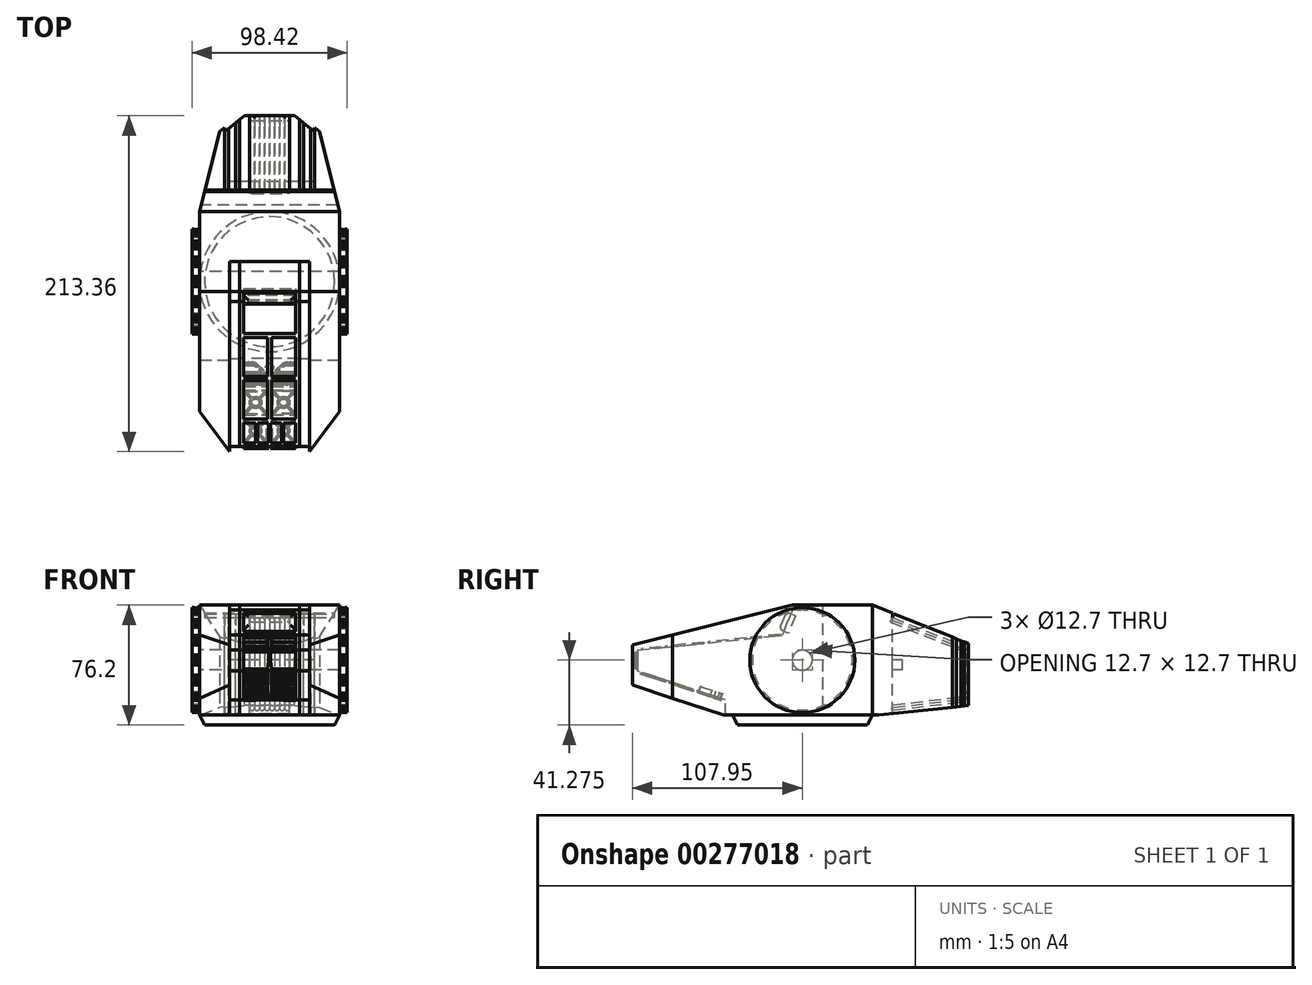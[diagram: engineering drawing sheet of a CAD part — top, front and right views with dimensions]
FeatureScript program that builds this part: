
annotation { "Feature Type Name" : "Feature", "Feature Type Description" : "" }
export const myFeature = defineFeature(function(context is Context, id is Id, definition is map)
    precondition{}
    {
        {
            var Q0;
            Q0=qCreatedBy(makeId("Top.planeOp"),FACE);
            cPlane(context, id + "F0", {"entities" : qUnion([Q0]), "cplaneType" : CPlaneType.OFFSET, "offset" : 38.1 * mm, "width" : 152.4 * mm, "height" : 152.4 * mm});
        }
        {
            var Q0;
            Q0=qCreatedBy(makeId("Front.planeOp"),FACE);
            cPlane(context, id + "F1", {"entities" : qUnion([Q0]), "cplaneType" : CPlaneType.OFFSET, "offset" : 165.1 * mm, "oppositeDirection" : true, "width" : 152.4 * mm, "height" : 152.4 * mm});
        }
        {
            var Q0;
            Q0=qCreatedBy(makeId("Top.planeOp"),FACE);
            cPlane(context, id + "F2", {"entities" : qUnion([Q0]), "cplaneType" : CPlaneType.OFFSET, "offset" : 38.1 * mm, "width" : 152.4 * mm, "height" : 152.4 * mm});
        }
        {
            var Q0;
            Q0=qCreatedBy(makeId("Right.planeOp"),FACE);
            cPlane(context, id + "F3", {"entities" : qUnion([Q0]), "cplaneType" : CPlaneType.OFFSET, "offset" : 44.45 * mm, "width" : 152.4 * mm, "height" : 152.4 * mm});
        }
        {
            var Q0;
            Q0=qCreatedBy(makeId("Top.planeOp"),FACE);
            cPlane(context, id + "F4", {"entities" : qUnion([Q0]), "cplaneType" : CPlaneType.OFFSET, "offset" : 38.1 * mm, "oppositeDirection" : true, "width" : 152.4 * mm, "height" : 152.4 * mm});
        }
        {
            var Q0;
            Q0=qCreatedBy(id+"F4.planeOp",FACE);
            cPlane(context, id + "F5", {"entities" : qUnion([Q0]), "cplaneType" : CPlaneType.OFFSET, "offset" : 6.35 * mm, "width" : 152.4 * mm, "height" : 152.4 * mm});
        }
        {
            var Q0;
            Q0=qCreatedBy(makeId("Top.planeOp"),FACE);
            var sketch = newSketch(context, id + "F6", { "sketchPlane" : qUnion([Q0])});
            skLineSegment(sketch, "E0", {"start": v(-19.05, 0) * mm, "end": v(19.05, 0) * mm});
            skLineSegment(sketch, "E1", {"start": v(0, 0) * mm, "end": v(0, 45.8) * mm});
            skPoint(sketch, "E1.endSnap0", {"position": v(0, 0) * mm});
            skLineSegment(sketch, "E2", {"start": v(-44.45, 25.4) * mm, "end": v(-44.45, 152.4) * mm});
            skLineSegment(sketch, "E3", {"start": v(44.45, 25.4) * mm, "end": v(44.45, 152.4) * mm});
            skLineSegment(sketch, "E4", {"start": v(-44.45, 152.4) * mm, "end": v(44.45, 152.4) * mm});
            skLineSegment(sketch, "E5", {"start": v(0, 152.4) * mm, "end": v(0, 215.9) * mm});
            skPoint(sketch, "E5.endSnap0", {"position": v(0, 152.4) * mm});
            skLineSegment(sketch, "E6", {"start": v(-15.88, 215.9) * mm, "end": v(15.87, 215.9) * mm});
            skLineSegment(sketch, "E7.0", {"start": v(-31.75, 203.2) * mm, "end": v(31.75, 203.2) * mm});
            skLineSegment(sketch, "E8", {"start": v(-44.45, 152.4) * mm, "end": v(-31.75, 203.2) * mm});
            skLineSegment(sketch, "E9", {"start": v(-15.88, 215.9) * mm, "end": v(-31.75, 203.2) * mm});
            skLineSegment(sketch, "E10", {"start": v(15.87, 215.9) * mm, "end": v(31.75, 203.2) * mm});
            skLineSegment(sketch, "E11", {"start": v(31.75, 203.2) * mm, "end": v(44.45, 152.4) * mm});
            skLineSegment(sketch, "E12", {"start": v(-19.05, 0) * mm, "end": v(-19.05, 120.65) * mm});
            skLineSegment(sketch, "E13", {"start": v(-19.05, 120.65) * mm, "end": v(19.05, 120.65) * mm});
            skLineSegment(sketch, "E14", {"start": v(19.05, 120.65) * mm, "end": v(19.05, 0) * mm});
            skLineSegment(sketch, "E15", {"start": v(-44.45, 25.4) * mm, "end": v(-25.4, 0) * mm});
            skLineSegment(sketch, "E16", {"start": v(19.05, 0) * mm, "end": v(25.4, 0) * mm});
            skLineSegment(sketch, "E17", {"start": v(25.4, 0) * mm, "end": v(44.45, 25.4) * mm});
            skLineSegment(sketch, "E18", {"start": v(-25.4, 0) * mm, "end": v(-19.05, 0) * mm});
            skSolve(sketch);
        }
        {
            var Q0;
            {var subQ1=sQuery(id+"F6.wireOp",EDGE,"E2");Q0=makeQuery(id+"F6.imprint","IMPRINT",FACE,{"disambiguationData":[TD([[makeQuery(id+"F6.imprint","IMPRINT",EDGE,{"derivedFrom":subQ1}),-1.0]])]});}
            extrude(context, id + "F7", {"entities" : qUnion([Q0]), "depth" : 76.2 * mm, "symmetric" : true});
        }
        {
            var Q0;
            Q0=qCreatedBy(makeId("Right.planeOp"),FACE);
            var sketch = newSketch(context, id + "F8", { "sketchPlane" : qUnion([Q0])});
            skLineSegment(sketch, "E19", {"start": v(0, 0) * mm, "end": v(101.6, 0) * mm});
            skLineSegment(sketch, "E20", {"start": v(101.6, 38.1) * mm, "end": v(101.6, -38.51) * mm});
            skLineSegment(sketch, "E21", {"start": v(0, 12.7) * mm, "end": v(0, -12.7) * mm});
            skLineSegment(sketch, "E22", {"start": v(0, 0) * mm, "end": v(107.95, 0) * mm});
            skLineSegment(sketch, "E23", {"start": v(107.95, 0) * mm, "end": v(107.95, -11.67) * mm});
            skLineSegment(sketch, "E24", {"start": v(63.5, -11.67) * mm, "end": v(152.4, -11.67) * mm});
            skLineSegment(sketch, "E25", {"start": v(63.5, -38.51) * mm, "end": v(59.18, -32.16) * mm});
            skLineSegment(sketch, "E26", {"start": v(0, -12.7) * mm, "end": v(59.18, -32.16) * mm});
            skLineSegment(sketch, "E27", {"start": v(0, 12.7) * mm, "end": v(101.6, 38.1) * mm});
            skLineSegment(sketch, "E28", {"start": v(152.4, -38.1) * mm, "end": v(156.72, -31.75) * mm});
            skLineSegment(sketch, "E29", {"start": v(152.4, 38.1) * mm, "end": v(215.9, 12.7) * mm});
            skLineSegment(sketch, "E30", {"start": v(156.72, -31.75) * mm, "end": v(215.9, -25.4) * mm});
            skLineSegment(sketch, "E31", {"start": v(215.9, -25.4) * mm, "end": v(215.9, 12.7) * mm});
            skLineSegment(sketch, "E32.bottom", {"start": v(0, 38.1) * mm, "end": v(215.9, 38.1) * mm});
            skLineSegment(sketch, "E32.top", {"start": v(0, -38.1) * mm, "end": v(215.9, -38.1) * mm});
            skLineSegment(sketch, "E32.left", {"start": v(0, 38.1) * mm, "end": v(0, -38.1) * mm});
            skLineSegment(sketch, "E32.right", {"start": v(215.9, 38.1) * mm, "end": v(215.9, -38.1) * mm});
            skLineSegment(sketch, "E33", {"start": v(215.9, 12.7) * mm, "end": v(215.9, -25.4) * mm});
            skLineSegment(sketch, "E34", {"start": v(152.4, 38.1) * mm, "end": v(156.72, -31.75) * mm});
            skLineSegment(sketch, "E35", {"start": v(221.8, 0) * mm, "end": v(221.8, 12.7) * mm});
            skPoint(sketch, "E35.startSnap0", {"position": v(215.9, 0) * mm});
            skLineSegment(sketch, "E36", {"start": v(221.8, 0) * mm, "end": v(221.8, -25.4) * mm});
            skLineSegment(sketch, "E37", {"start": v(63.5, -38.51) * mm, "end": v(63.5, -43.93) * mm});
            skLineSegment(sketch, "E38", {"start": v(63.5, -43.93) * mm, "end": v(152.4, -43.93) * mm});
            skLineSegment(sketch, "E39", {"start": v(107.95, -43.93) * mm, "end": v(107.95, 70.13) * mm});
            skLineSegment(sketch, "E40", {"start": v(59.18, -32.16) * mm, "end": v(156.72, -31.75) * mm});
            skSolve(sketch);
        }
        {
            var Q0;
            {var subQ0=sQuery(id+"F6.wireOp",EDGE,"E12");Q0=makeQuery(id+"F6.imprint","IMPRINT",FACE,{"disambiguationData":[TD([[makeQuery(id+"F6.imprint","IMPRINT",EDGE,{"derivedFrom":subQ0}),-1.0]])]});}
            extrude(context, id + "F9", {"entities" : qUnion([Q0]), "depth" : 76.2 * mm, "symmetric" : true});
        }
        {
            var Q0;
            {var subQ5=sQuery(id+"F6.wireOp",EDGE,"E9");Q0=makeQuery(id+"F6.imprint","IMPRINT",FACE,{"disambiguationData":[TD([[makeQuery(id+"F6.imprint","IMPRINT",EDGE,{"derivedFrom":subQ5}),1.0]])]});}
            var Q1;
            {var subQ5=sQuery(id+"F6.wireOp",EDGE,"E10");Q1=makeQuery(id+"F6.imprint","IMPRINT",FACE,{"disambiguationData":[TD([[makeQuery(id+"F6.imprint","IMPRINT",EDGE,{"derivedFrom":subQ5}),-1.0]])]});}
            var Q2;
            {var subQ0=sQuery(id+"F6.wireOp",EDGE,"E8");Q2=makeQuery(id+"F6.imprint","IMPRINT",FACE,{"disambiguationData":[TD([[makeQuery(id+"F6.imprint","IMPRINT",EDGE,{"derivedFrom":subQ0}),-1.0]])]});}
            var Q3;
            {var subQ0=sQuery(id+"F6.wireOp",EDGE,"E11");Q3=makeQuery(id+"F6.imprint","IMPRINT",FACE,{"disambiguationData":[TD([[makeQuery(id+"F6.imprint","IMPRINT",EDGE,{"derivedFrom":subQ0}),-1.0]])]});}
            extrude(context, id + "F10", {"entities" : qUnion([Q0, Q1, Q2, Q3]), "depth" : 76.2 * mm, "symmetric" : true});
        }
        {
            var Q0;
            {var subQ0=sQuery(id+"F8.wireOp",EDGE,"E32.right");var subQ1=sQuery(id+"F8.wireOp",EDGE,"3308d05f-1129-43a6-b52a-610bf1bbaef7");var subQ2=makeQuery(id+"F8.imprint","INTERSECT",VERTEX,{"derivedFrom":[subQ1,subQ0]});Q0=makeQuery(id+"F8.imprint","IMPRINT",FACE,{"disambiguationData":[TD([[makeQuery(id+"F8.imprint","IMPRINT",EDGE,{"disambiguationData":[TD([[subQ2,1.0]])],"derivedFrom":subQ1}),1.0]])]});}
            var Q1;
            {var subQ6=sQuery(id+"F8.wireOp",EDGE,"E28");Q1=makeQuery(id+"F8.imprint","IMPRINT",FACE,{"disambiguationData":[TD([[makeQuery(id+"F8.imprint","IMPRINT",EDGE,{"derivedFrom":subQ6}),-1.0]])]});}
            var Q2;
            {var subQ0=sQuery(id+"F8.wireOp",EDGE,"E29");Q2=makeQuery(id+"F8.imprint","IMPRINT",FACE,{"disambiguationData":[TD([[makeQuery(id+"F8.imprint","IMPRINT",EDGE,{"derivedFrom":subQ0}),1.0]])]});}
            var Q3;
            {var subQ0=sQuery(id+"F8.wireOp",EDGE,"E27");Q3=makeQuery(id+"F8.imprint","IMPRINT",FACE,{"disambiguationData":[TD([[makeQuery(id+"F8.imprint","IMPRINT",EDGE,{"derivedFrom":subQ0}),1.0]])]});}
            var Q4;
            {var subQ0=sQuery(id+"F8.wireOp",EDGE,"E26");Q4=makeQuery(id+"F8.imprint","IMPRINT",FACE,{"disambiguationData":[TD([[makeQuery(id+"F8.imprint","IMPRINT",EDGE,{"derivedFrom":subQ0}),-1.0]])]});}
            extrude(context, id + "F11", {"entities" : qUnion([Q0, Q1, Q2, Q3, Q4]), "depth" : 101.6 * mm, "symmetric" : true});
        }
        {
            var Q0;
            Q0=makeQuery(id+"F11.opExtrude","SWEPT_BODY",BODY,{"disambiguationData":[OSD([sQuery(id+"F8.wireOp",EDGE,"E29"),sQuery(id+"F8.wireOp",EDGE,"E32.bottom"),sQuery(id+"F8.wireOp",EDGE,"E32.right")])]});
            var Q1;
            Q1=makeQuery(id+"F11.opExtrude","SWEPT_BODY",BODY,{"disambiguationData":[OSD([sQuery(id+"F8.wireOp",EDGE,"E28"),sQuery(id+"F8.wireOp",EDGE,"E30"),sQuery(id+"F8.wireOp",EDGE,"E31"),sQuery(id+"F8.wireOp",EDGE,"E32.top"),sQuery(id+"F8.wireOp",EDGE,"E32.right")])]});
            var Q2;
            Q2=makeQuery(id+"F11.opExtrude","SWEPT_BODY",BODY,{"disambiguationData":[OSD([sQuery(id+"F8.wireOp",EDGE,"E27"),sQuery(id+"F8.wireOp",EDGE,"E32.bottom"),sQuery(id+"F8.wireOp",EDGE,"E32.left")])]});
            var Q3;
            Q3=makeQuery(id+"F11.opExtrude","SWEPT_BODY",BODY,{"disambiguationData":[OSD([sQuery(id+"F8.wireOp",EDGE,"E25"),sQuery(id+"F8.wireOp",EDGE,"E26"),sQuery(id+"F8.wireOp",EDGE,"E32.top"),sQuery(id+"F8.wireOp",EDGE,"E32.left")])]});
            var Q4;
            Q4=makeQuery(id+"F7.opExtrude","SWEPT_BODY",BODY,{"disambiguationData":[OSD([sQuery(id+"F6.wireOp",EDGE,"E2"),sQuery(id+"F6.wireOp",EDGE,"E3"),sQuery(id+"F6.wireOp",EDGE,"E4"),sQuery(id+"F6.wireOp",EDGE,"E12"),sQuery(id+"F6.wireOp",EDGE,"E13"),sQuery(id+"F6.wireOp",EDGE,"E14"),sQuery(id+"F6.wireOp",EDGE,"E15"),sQuery(id+"F6.wireOp",EDGE,"E16"),sQuery(id+"F6.wireOp",EDGE,"E17"),sQuery(id+"F6.wireOp",EDGE,"E18")])]});
            var Q5;
            Q5=makeQuery(id+"F9.opExtrude","SWEPT_BODY",BODY,{"disambiguationData":[OSD([sQuery(id+"F6.wireOp",EDGE,"E0"),sQuery(id+"F6.wireOp",EDGE,"E12"),sQuery(id+"F6.wireOp",EDGE,"E13"),sQuery(id+"F6.wireOp",EDGE,"E14")])]});
            var Q6;
            Q6=makeQuery(id+"F10.opExtrude","SWEPT_BODY",BODY,{"disambiguationData":[OSD([sQuery(id+"F6.wireOp",EDGE,"E4"),sQuery(id+"F6.wireOp",EDGE,"E6"),sQuery(id+"F6.wireOp",EDGE,"E8"),sQuery(id+"F6.wireOp",EDGE,"E9"),sQuery(id+"F6.wireOp",EDGE,"E10"),sQuery(id+"F6.wireOp",EDGE,"E11")])]});
            booleanBodies(context, id + "F12", {"operationType" : BooleanOperationType.SUBTRACTION, "tools" : qUnion([Q0, Q1, Q2, Q3]), "targets" : qUnion([Q4, Q5, Q6])});
        }
        {
            var Q0;
            Q0=qCreatedBy(makeId("Right.planeOp"),FACE);
            var sketch = newSketch(context, id + "F13", { "sketchPlane" : qUnion([Q0])});
            skLineSegment(sketch, "E41", {"start": v(3.17, 9.52) * mm, "end": v(95.25, 19.05) * mm});
            skLineSegment(sketch, "E42", {"start": v(101.6, 34.93) * mm, "end": v(95.25, 19.05) * mm});
            skLineSegment(sketch, "E43", {"start": v(101.6, 34.93) * mm, "end": v(120.65, 38.1) * mm});
            skLineSegment(sketch, "E44", {"start": v(3.17, 9.52) * mm, "end": v(3.17, -3.72) * mm});
            skLineSegment(sketch, "E45.0", {"start": v(59.18, -22.14) * mm, "end": v(2.98, -3.65) * mm});
            skLineSegment(sketch, "E46", {"start": v(59.18, -32.06) * mm, "end": v(59.18, -22.14) * mm});
            skLineSegment(sketch, "E47", {"start": v(120.65, 38.1) * mm, "end": v(0, 40.38) * mm});
            skLineSegment(sketch, "E48", {"start": v(0, 40.38) * mm, "end": v(0, -32.06) * mm});
            skLineSegment(sketch, "E49", {"start": v(0, -32.06) * mm, "end": v(59.18, -32.06) * mm});
            skSolve(sketch);
        }
        {
            var Q0;
            Q0 = qSketchRegion(id + "F13", true);
            extrude(context, id + "F14", {"entities" : qUnion([Q0]), "operationType" : NewBodyOperationType.REMOVE, "depth" : 50.8 * mm, "symmetric" : true});
        }
        {
            var Q0;
            Q0=qCreatedBy(id+"F0.planeOp",FACE);
            var sketch = newSketch(context, id + "F15", { "sketchPlane" : qUnion([Q0])});
            skLineSegment(sketch, "E50", {"start": v(0, 0) * mm, "end": v(0, 165.1) * mm});
            skLineSegment(sketch, "E51", {"start": v(-44.45, 152.4) * mm, "end": v(74.49, 152.4) * mm});
            skLineSegment(sketch, "E52", {"start": v(-19.05, 213.36) * mm, "end": v(-19.05, 165.1) * mm});
            skLineSegment(sketch, "E53", {"start": v(-21.6, 211.33) * mm, "end": v(-21.6, 165.1) * mm});
            skLineSegment(sketch, "E54", {"start": v(-28.58, 205.74) * mm, "end": v(-26.04, 207.77) * mm});
            skPoint(sketch, "E55.orphan", {"position": v(-28.58, 259.23) * mm});
            skPoint(sketch, "E56.orphan", {"position": v(-26.04, 263.6) * mm});
            skPoint(sketch, "E57.orphan", {"position": v(-21.6, 218.8) * mm});
            skPoint(sketch, "E58.orphan", {"position": v(-19.05, 223.69) * mm});
            skLineSegment(sketch, "E59", {"start": v(-28.58, 165.1) * mm, "end": v(-26.04, 165.1) * mm});
            skPoint(sketch, "E60.orphan", {"position": v(-78.7, 165.1) * mm});
            skLineSegment(sketch, "E61.trimOffspring", {"start": v(-28.58, 165.1) * mm, "end": v(-28.58, 205.74) * mm});
            skLineSegment(sketch, "E62.trimOffspring", {"start": v(-26.04, 165.1) * mm, "end": v(-26.04, 207.77) * mm});
            skLineSegment(sketch, "E63.trimOffspring", {"start": v(-21.6, 165.1) * mm, "end": v(-19.05, 165.1) * mm});
            skPoint(sketch, "E64.orphan", {"position": v(-31.75, 203.2) * mm});
            skLineSegment(sketch, "E65.trimOffspring", {"start": v(-21.6, 211.33) * mm, "end": v(-19.05, 213.36) * mm});
            skPoint(sketch, "E66.orphan", {"position": v(-15.88, 215.9) * mm});
            skLineSegment(sketch, "E67.MirrorCS", {"start": v(19.05, 213.36) * mm, "end": v(19.05, 165.1) * mm});
            skLineSegment(sketch, "E68.MirrorCS", {"start": v(21.6, 211.33) * mm, "end": v(21.6, 165.1) * mm});
            skLineSegment(sketch, "E69.MirrorCS", {"start": v(26.04, 165.1) * mm, "end": v(26.04, 207.77) * mm});
            skLineSegment(sketch, "E70.MirrorCS", {"start": v(28.58, 165.1) * mm, "end": v(28.58, 205.74) * mm});
            skLineSegment(sketch, "E71.MirrorCS", {"start": v(21.6, 165.1) * mm, "end": v(19.05, 165.1) * mm});
            skLineSegment(sketch, "E72.MirrorCS", {"start": v(28.58, 165.1) * mm, "end": v(26.04, 165.1) * mm});
            skLineSegment(sketch, "E73", {"start": v(-12.7, 215.9) * mm, "end": v(-12.7, 165.1) * mm});
            skLineSegment(sketch, "E74.MirrorCS", {"start": v(12.7, 215.9) * mm, "end": v(12.7, 165.1) * mm});
            skLineSegment(sketch, "E75", {"start": v(-12.7, 165.1) * mm, "end": v(12.7, 165.1) * mm});
            skPoint(sketch, "E76.orphan", {"position": v(-12.7, 158.24) * mm});
            skPoint(sketch, "E77.orphan", {"position": v(12.7, 158.24) * mm});
            skPoint(sketch, "E78.orphan", {"position": v(0, 215.9) * mm});
            skLineSegment(sketch, "E79", {"start": v(-12.7, 215.9) * mm, "end": v(12.7, 215.9) * mm});
            skLineSegment(sketch, "E80", {"start": v(19.05, 213.36) * mm, "end": v(21.6, 211.33) * mm});
            skLineSegment(sketch, "E81", {"start": v(26.04, 207.77) * mm, "end": v(28.58, 205.74) * mm});
            skSolve(sketch);
        }
        {
            var Q0;
            Q0 = qSketchRegion(id + "F15", true);
            extrude(context, id + "F16", {"entities" : qUnion([Q0]), "operationType" : NewBodyOperationType.REMOVE, "oppositeDirection" : true, "depth" : 76.2 * mm});
        }
        {
            var Q0;
            Q0 = qSketchRegion(id + "F15", true);
            extrude(context, id + "F17", {"entities" : qUnion([Q0]), "oppositeDirection" : true, "depth" : 76.2 * mm});
        }
        {
            var Q0;
            {var subQ0=sQuery(id+"F8.wireOp",EDGE,"E29");Q0=makeQuery(id+"F8.imprint","IMPRINT",FACE,{"disambiguationData":[TD([[makeQuery(id+"F8.imprint","IMPRINT",EDGE,{"derivedFrom":subQ0}),1.0]])]});}
            var Q1;
            {var subQ8=sQuery(id+"F8.wireOp",EDGE,"E28");Q1=makeQuery(id+"F8.imprint","IMPRINT",FACE,{"disambiguationData":[TD([[makeQuery(id+"F8.imprint","IMPRINT",EDGE,{"derivedFrom":subQ8}),-1.0]])]});}
            var Q2;
            {var subQ0=sQuery(id+"F8.wireOp",EDGE,"E32.right");var subQ1=sQuery(id+"F8.wireOp",EDGE,"3308d05f-1129-43a6-b52a-610bf1bbaef7");var subQ2=makeQuery(id+"F8.imprint","INTERSECT",VERTEX,{"derivedFrom":[subQ1,subQ0]});Q2=makeQuery(id+"F8.imprint","IMPRINT",FACE,{"disambiguationData":[TD([[makeQuery(id+"F8.imprint","IMPRINT",EDGE,{"disambiguationData":[TD([[subQ2,1.0]])],"derivedFrom":subQ1}),1.0]])]});}
            extrude(context, id + "F18", {"entities" : qUnion([Q0, Q1, Q2]), "depth" : 76.2 * mm, "symmetric" : true});
        }
        {
            var Q0;
            Q0=makeQuery(id+"F18.opExtrude","SWEPT_BODY",BODY,{"disambiguationData":[OSD([sQuery(id+"F8.wireOp",EDGE,"E29"),sQuery(id+"F8.wireOp",EDGE,"E32.bottom"),sQuery(id+"F8.wireOp",EDGE,"E32.right")])]});
            var Q1;
            Q1=makeQuery(id+"F18.opExtrude","SWEPT_BODY",BODY,{"disambiguationData":[OSD([sQuery(id+"F8.wireOp",EDGE,"E28"),sQuery(id+"F8.wireOp",EDGE,"E30"),sQuery(id+"F8.wireOp",EDGE,"E31"),sQuery(id+"F8.wireOp",EDGE,"E32.top"),sQuery(id+"F8.wireOp",EDGE,"E32.right")])]});
            var Q2;
            Q2=makeQuery(id+"F17.opExtrude","SWEPT_BODY",BODY,{"disambiguationData":[OSD([sQuery(id+"F15.wireOp",EDGE,"E54"),sQuery(id+"F15.wireOp",EDGE,"E59"),sQuery(id+"F15.wireOp",EDGE,"E61.trimOffspring"),sQuery(id+"F15.wireOp",EDGE,"E62.trimOffspring")])]});
            var Q3;
            Q3=makeQuery(id+"F17.opExtrude","SWEPT_BODY",BODY,{"disambiguationData":[OSD([sQuery(id+"F15.wireOp",EDGE,"E52"),sQuery(id+"F15.wireOp",EDGE,"E53"),sQuery(id+"F15.wireOp",EDGE,"E63.trimOffspring"),sQuery(id+"F15.wireOp",EDGE,"E65.trimOffspring")])]});
            var Q4;
            Q4=makeQuery(id+"F17.opExtrude","SWEPT_BODY",BODY,{"disambiguationData":[OSD([sQuery(id+"F15.wireOp",EDGE,"E73"),sQuery(id+"F15.wireOp",EDGE,"E74.MirrorCS"),sQuery(id+"F15.wireOp",EDGE,"E75"),sQuery(id+"F15.wireOp",EDGE,"E79")])]});
            var Q5;
            Q5=makeQuery(id+"F17.opExtrude","SWEPT_BODY",BODY,{"disambiguationData":[OSD([sQuery(id+"F15.wireOp",EDGE,"E67.MirrorCS"),sQuery(id+"F15.wireOp",EDGE,"E68.MirrorCS"),sQuery(id+"F15.wireOp",EDGE,"E71.MirrorCS"),sQuery(id+"F15.wireOp",EDGE,"E80")])]});
            var Q6;
            Q6=makeQuery(id+"F17.opExtrude","SWEPT_BODY",BODY,{"disambiguationData":[OSD([sQuery(id+"F15.wireOp",EDGE,"E69.MirrorCS"),sQuery(id+"F15.wireOp",EDGE,"E70.MirrorCS"),sQuery(id+"F15.wireOp",EDGE,"E72.MirrorCS"),sQuery(id+"F15.wireOp",EDGE,"E81")])]});
            booleanBodies(context, id + "F19", {"operationType" : BooleanOperationType.SUBTRACTION, "tools" : qUnion([Q0, Q1]), "targets" : qUnion([Q2, Q3, Q4, Q5, Q6])});
        }
        {
            var Q0;
            Q0=makeQuery(id+"F17.opExtrude","SWEPT_FACE",FACE,{"disambiguationData":[OSD([sQuery(id+"F15.wireOp",EDGE,"E75")])]});
            var sketch = newSketch(context, id + "F20", { "sketchPlane" : qUnion([Q0])});
            skLineSegment(sketch, "E82.bottom", {"start": v(28.58, -3.17) * mm, "end": v(-28.58, -3.18) * mm});
            skLineSegment(sketch, "E82.top", {"start": v(28.58, 3.18) * mm, "end": v(-28.58, 3.17) * mm});
            skLineSegment(sketch, "E82.left", {"start": v(28.58, -3.17) * mm, "end": v(28.58, 3.18) * mm});
            skLineSegment(sketch, "E82.right", {"start": v(-28.58, -3.18) * mm, "end": v(-28.58, 3.17) * mm});
            skPoint(sketch, "E82.middle", {"position": v(0, 0) * mm});
            skSolve(sketch);
        }
        {
            var Q0;
            Q0 = qSketchRegion(id + "F20", true);
            extrude(context, id + "F21", {"entities" : qUnion([Q0]), "oppositeDirection" : true, "depth" : 6.35 * mm});
        }
        {
            var Q0;
            Q0=qCreatedBy(id+"F1.planeOp",FACE);
            var sketch = newSketch(context, id + "F22", { "sketchPlane" : qUnion([Q0])});
            skLineSegment(sketch, "E83.bottom", {"start": v(28.58, 3.18) * mm, "end": v(-28.58, 3.18) * mm});
            skLineSegment(sketch, "E83.top", {"start": v(28.57, -3.18) * mm, "end": v(-28.58, -3.18) * mm});
            skLineSegment(sketch, "E83.left", {"start": v(28.57, 3.18) * mm, "end": v(28.57, -3.18) * mm});
            skLineSegment(sketch, "E83.right", {"start": v(-28.58, 3.18) * mm, "end": v(-28.58, -3.18) * mm});
            skPoint(sketch, "E83.middle", {"position": v(0, 0) * mm});
            skSolve(sketch);
        }
        {
            var Q0;
            Q0 = qSketchRegion(id + "F22", true);
            extrude(context, id + "F23", {"entities" : qUnion([Q0]), "oppositeDirection" : true, "depth" : 6.35 * mm});
        }
        {
            var Q0;
            Q0=makeQuery(id+"F23.opExtrude","SWEPT_BODY",BODY,{"disambiguationData":[OSD([sQuery(id+"F22.wireOp",EDGE,"E83.bottom"),sQuery(id+"F22.wireOp",EDGE,"E83.top"),sQuery(id+"F22.wireOp",EDGE,"E83.left"),sQuery(id+"F22.wireOp",EDGE,"E83.right")])]});
            var Q1;
            Q1=makeQuery(id+"F10.opExtrude","SWEPT_BODY",BODY,{"disambiguationData":[OSD([sQuery(id+"F6.wireOp",EDGE,"E4"),sQuery(id+"F6.wireOp",EDGE,"E6"),sQuery(id+"F6.wireOp",EDGE,"E8"),sQuery(id+"F6.wireOp",EDGE,"E9"),sQuery(id+"F6.wireOp",EDGE,"E10"),sQuery(id+"F6.wireOp",EDGE,"E11")])]});
            booleanBodies(context, id + "F24", {"operationType" : BooleanOperationType.SUBTRACTION, "tools" : qUnion([Q0]), "targets" : qUnion([Q1])});
        }
        {
            var Q0;
            Q0=qCreatedBy(id+"F2.planeOp",FACE);
            var sketch = newSketch(context, id + "F25", { "sketchPlane" : qUnion([Q0])});
            skLineSegment(sketch, "E84", {"start": v(15.87, 215.9) * mm, "end": v(-15.88, 215.9) * mm});
            skLineSegment(sketch, "E85", {"start": v(28.57, 205.74) * mm, "end": v(15.87, 215.9) * mm});
            skLineSegment(sketch, "E86", {"start": v(-15.88, 215.9) * mm, "end": v(-28.58, 205.74) * mm});
            skLineSegment(sketch, "E87", {"start": v(-28.58, 203.2) * mm, "end": v(-28.58, 205.74) * mm});
            skLineSegment(sketch, "E88.0", {"start": v(15.87, 213.36) * mm, "end": v(-15.88, 213.36) * mm});
            skLineSegment(sketch, "E89", {"start": v(28.57, 205.74) * mm, "end": v(28.57, 203.2) * mm});
            skLineSegment(sketch, "E90", {"start": v(-28.58, 203.2) * mm, "end": v(-15.88, 213.36) * mm});
            skLineSegment(sketch, "E91", {"start": v(15.87, 213.36) * mm, "end": v(28.57, 203.2) * mm});
            skSolve(sketch);
        }
        {
            var Q0;
            Q0=makeQuery(id+"F25.imprint","IMPRINT",FACE,{"disambiguationData":[TD([[makeQuery(id+"F25.imprint","IMPRINT",EDGE,{"derivedFrom":sQuery(id+"F25.wireOp",EDGE,"E84")}),1.0]])]});
            extrude(context, id + "F26", {"entities" : qUnion([Q0]), "operationType" : NewBodyOperationType.REMOVE, "endBound" : BoundingType.THROUGH_ALL, "oppositeDirection" : true, "depth" : 25.4 * mm});
        }
        {
            var Q0;
            Q0=qCreatedBy(id+"F3.planeOp",FACE);
            var sketch = newSketch(context, id + "F27", { "sketchPlane" : qUnion([Q0])});
            skLineSegment(sketch, "E92", {"start": v(215.9, -55.54) * mm, "end": v(165.1, -55.54) * mm});
            skLineSegment(sketch, "E93", {"start": v(165.1, -31.32) * mm, "end": v(165.1, 33.02) * mm});
            skLineSegment(sketch, "E94", {"start": v(215.9, 0) * mm, "end": v(215.9, 12.7) * mm});
            skLineSegment(sketch, "E95", {"start": v(215.9, 0) * mm, "end": v(215.9, -25.4) * mm});
            skLineSegment(sketch, "E96", {"start": v(0, 38.1) * mm, "end": v(152.4, 38.1) * mm});
            skLineSegment(sketch, "E97", {"start": v(165.1, 33.02) * mm, "end": v(215.9, 12.7) * mm});
            skLineSegment(sketch, "E98", {"start": v(0, -38.1) * mm, "end": v(157.1, -38.1) * mm});
            skLineSegment(sketch, "E99", {"start": v(157.1, -38.1) * mm, "end": v(157.1, -32.26) * mm});
            skLineSegment(sketch, "E100", {"start": v(165.1, -31.32) * mm, "end": v(215.9, -25.4) * mm});
            skPoint(sketch, "E101.orphan", {"position": v(0, 0) * mm});
            skLineSegment(sketch, "E102.0", {"start": v(165.1, 30.28) * mm, "end": v(209.37, 12.58) * mm});
            skLineSegment(sketch, "E103.0", {"start": v(165.1, -28.77) * mm, "end": v(207.75, -23.8) * mm});
            skLineSegment(sketch, "E104", {"start": v(214.96, 10.34) * mm, "end": v(215.9, 9.96) * mm});
            skLineSegment(sketch, "E105", {"start": v(215.6, -22.88) * mm, "end": v(215.9, -22.84) * mm});
            skLineSegment(sketch, "E106.0", {"start": v(213.36, 0) * mm, "end": v(213.36, -17.49) * mm});
            skLineSegment(sketch, "E107.0", {"start": v(213.36, 0) * mm, "end": v(213.36, 6.68) * mm});
            skLineSegment(sketch, "E108", {"start": v(165.1, 30.28) * mm, "end": v(164.16, 30.66) * mm});
            skLineSegment(sketch, "E109", {"start": v(165.1, 33.02) * mm, "end": v(164.16, 30.66) * mm});
            skLineSegment(sketch, "E110", {"start": v(165.1, 33.02) * mm, "end": v(168.5, 41.5) * mm});
            skLineSegment(sketch, "E111", {"start": v(168.5, 41.5) * mm, "end": v(156.55, 41.5) * mm});
            skLineSegment(sketch, "E112", {"start": v(156.55, 41.5) * mm, "end": v(156.55, -26.27) * mm});
            skLineSegment(sketch, "E113", {"start": v(165.1, -31.32) * mm, "end": v(165.43, -34.12) * mm});
            skLineSegment(sketch, "E114", {"start": v(165.43, -34.12) * mm, "end": v(156.55, -26.27) * mm});
            skPoint(sketch, "E115.trimOffspring.end.orphan", {"position": v(156.55, -29.76) * mm});
            skPoint(sketch, "E116.end.orphan", {"position": v(164.8, -28.77) * mm});
            skLineSegment(sketch, "E117", {"start": v(165.1, -31.32) * mm, "end": v(164.8, -28.77) * mm});
            skLineSegment(sketch, "E118", {"start": v(165.1, -28.77) * mm, "end": v(164.8, -28.8) * mm});
            skLineSegment(sketch, "E119", {"start": v(165.1, 30.28) * mm, "end": v(169.41, 41.07) * mm});
            skLineSegment(sketch, "E120", {"start": v(169.41, 41.07) * mm, "end": v(168.5, 41.5) * mm});
            skPoint(sketch, "E121.newPointB", {"position": v(213.36, 10.98) * mm});
            skArc(sketch, "E121.filletArc", {"start": v(213.36, 6.68) * mm, "mid": v(212.27, 10.24) * mm, "end": v(209.37, 12.58) * mm});
            skPoint(sketch, "E122.newPointB", {"position": v(213.36, -23.14) * mm});
            skArc(sketch, "E122.filletArc", {"start": v(207.75, -23.8) * mm, "mid": v(211.75, -21.7) * mm, "end": v(213.36, -17.49) * mm});
            skSolve(sketch);
        }
        {
            var Q0;
            {var subQ1=sQuery(id+"F27.wireOp",EDGE,"E97");Q0=makeQuery(id+"F27.imprint","IMPRINT",FACE,{"disambiguationData":[TD([[makeQuery(id+"F27.imprint","IMPRINT",EDGE,{"derivedFrom":subQ1}),-1.0]])]});}
            var Q1;
            {var subQ1=sQuery(id+"F27.wireOp",EDGE,"E100");Q1=makeQuery(id+"F27.imprint","IMPRINT",FACE,{"disambiguationData":[TD([[makeQuery(id+"F27.imprint","IMPRINT",EDGE,{"derivedFrom":subQ1}),1.0]])]});}
            var Q2;
            {var subQ8=sQuery(id+"F27.wireOp",EDGE,"E104");Q2=makeQuery(id+"F27.imprint","IMPRINT",FACE,{"disambiguationData":[TD([[makeQuery(id+"F27.imprint","IMPRINT",EDGE,{"derivedFrom":subQ8}),1.0]])]});}
            var Q3;
            {var subQ6=sQuery(id+"F27.wireOp",EDGE,"E104");Q3=makeQuery(id+"F27.imprint","IMPRINT",FACE,{"disambiguationData":[TD([[makeQuery(id+"F27.imprint","IMPRINT",EDGE,{"derivedFrom":subQ6}),-1.0]])]});}
            extrude(context, id + "F28", {"entities" : qUnion([Q0, Q1, Q2, Q3]), "operationType" : NewBodyOperationType.REMOVE, "endBound" : BoundingType.THROUGH_ALL, "oppositeDirection" : true, "depth" : 25.4 * mm});
        }
        {
            var Q0;
            {var subQ0=sQuery(id+"F27.wireOp",EDGE,"E108");Q0=makeQuery(id+"F27.imprint","IMPRINT",FACE,{"disambiguationData":[TD([[makeQuery(id+"F27.imprint","IMPRINT",EDGE,{"derivedFrom":subQ0}),1.0]])]});}
            var Q1;
            {var subQ0=sQuery(id+"F27.wireOp",EDGE,"E110");Q1=makeQuery(id+"F27.imprint","IMPRINT",FACE,{"disambiguationData":[TD([[makeQuery(id+"F27.imprint","IMPRINT",EDGE,{"derivedFrom":subQ0}),-1.0]])]});}
            extrude(context, id + "F29", {"entities" : qUnion([Q0, Q1]), "oppositeDirection" : true, "depth" : 88.9 * mm});
        }
        {
            var Q0;
            Q0=makeQuery(id+"F28.boolean.opBoolean","COPY",FACE,{"disambiguationData":[TD([makeQuery(id+"F17.opExtrude","SWEPT_FACE",FACE,{"disambiguationData":[OSD([sQuery(id+"F15.wireOp",EDGE,"E73")])]})])],"derivedFrom":makeQuery(id+"F28.opExtrude","SWEPT_FACE",FACE,{"disambiguationData":[OSD([sQuery(id+"F27.wireOp",EDGE,"E103.0"),sQuery(id+"F27.wireOp",EDGE,"E105")])]})});
            var sketch = newSketch(context, id + "F30", { "sketchPlane" : qUnion([Q0])});
            skLineSegment(sketch, "E123.0", {"start": v(11.11, -209.24) * mm, "end": v(11.11, -160.66) * mm});
            skSolve(sketch);
        }
        {
            var Q0;
            Q0=makeQuery(id+"F29.opExtrude","SWEPT_FACE",FACE,{"disambiguationData":[OSD([sQuery(id+"F27.wireOp",EDGE,"E119")])]});
            var sketch = newSketch(context, id + "F31", { "sketchPlane" : qUnion([Q0])});
            skLineSegment(sketch, "E124", {"start": v(0, 91.97) * mm, "end": v(0, 97.74) * mm});
            skPoint(sketch, "E124.endSnap0", {"position": v(0, 91.97) * mm});
            skArc(sketch, "E125", {"start": v(-9.52, 87.85) * mm, "mid": v(-12.24, 88.97) * mm, "end": v(-11.11, 86.26) * mm});
            skArc(sketch, "E126.1.0.0", {"start": v(-6.35, 87.85) * mm, "mid": v(-7.94, 89.43) * mm, "end": v(-9.52, 87.85) * mm});
            skArc(sketch, "E126.2.0.0", {"start": v(-3.17, 87.85) * mm, "mid": v(-4.76, 89.43) * mm, "end": v(-6.35, 87.85) * mm});
            skArc(sketch, "E126.3.0.0", {"start": v(0, 87.85) * mm, "mid": v(-1.59, 89.43) * mm, "end": v(-3.17, 87.85) * mm});
            skArc(sketch, "E126.4.0.0", {"start": v(3.18, 87.85) * mm, "mid": v(1.59, 89.43) * mm, "end": v(0, 87.85) * mm});
            skArc(sketch, "E126.5.0.0", {"start": v(6.35, 87.85) * mm, "mid": v(4.76, 89.43) * mm, "end": v(3.18, 87.85) * mm});
            skArc(sketch, "E126.6.0.0", {"start": v(9.53, 87.85) * mm, "mid": v(7.94, 89.43) * mm, "end": v(6.35, 87.85) * mm});
            skArc(sketch, "E126.7.0.0", {"start": v(11.11, 86.26) * mm, "mid": v(12.24, 88.97) * mm, "end": v(9.53, 87.85) * mm});
            skLineSegment(sketch, "E126.direction1", {"start": v(-11.11, 87.85) * mm, "end": v(-7.94, 87.85) * mm, "construction": true});
            skLineSegment(sketch, "E127.bottom", {"start": v(-12.7, 91.17) * mm, "end": v(12.7, 91.17) * mm});
            skLineSegment(sketch, "E127.top", {"start": v(-12.7, 87.85) * mm, "end": v(12.7, 87.85) * mm});
            skLineSegment(sketch, "E127.left", {"start": v(-12.7, 91.17) * mm, "end": v(-12.7, 87.85) * mm});
            skLineSegment(sketch, "E127.right", {"start": v(12.7, 91.17) * mm, "end": v(12.7, 87.85) * mm});
            skLineSegment(sketch, "E128.bottom", {"start": v(11.11, 87.85) * mm, "end": v(-11.11, 87.85) * mm});
            skLineSegment(sketch, "E128.top", {"start": v(11.11, 86.26) * mm, "end": v(-11.11, 86.26) * mm});
            skLineSegment(sketch, "E128.right", {"start": v(-11.11, 87.85) * mm, "end": v(-11.11, 86.26) * mm});
            skSolve(sketch);
        }
        {
            var Q0;
            Q0=makeQuery(id+"F31.imprint","IMPRINT",FACE,{"disambiguationData":[TD([[makeQuery(id+"F31.imprint","IMPRINT",EDGE,{"derivedFrom":sQuery(id+"F31.wireOp",EDGE,"E127.bottom")}),-1.0]])]});
            var Q1;
            {var subQ0=sQuery(id+"F31.wireOp",EDGE,"E127.top");var subQ1=sQuery(id+"F31.wireOp",EDGE,"E125");var subQ2=makeQuery(id+"F31.imprint","INTERSECT",VERTEX,{"derivedFrom":[subQ1,subQ0,sQuery(id+"F31.wireOp",EDGE,"E127.left")]});Q1=makeQuery(id+"F31.imprint","IMPRINT",FACE,{"disambiguationData":[TD([[makeQuery(id+"F31.imprint","IMPRINT",EDGE,{"disambiguationData":[TD([[subQ2,-1.0]])],"derivedFrom":subQ1}),1.0]])]});}
            var Q2;
            {var subQ0=sQuery(id+"F31.wireOp",EDGE,"E127.top");var subQ1=sQuery(id+"F31.wireOp",EDGE,"E126.1.0.0");var subQ2=makeQuery(id+"F31.imprint","INTERSECT",VERTEX,{"derivedFrom":[sQuery(id+"F31.wireOp",EDGE,"E125"),subQ1,subQ0]});Q2=makeQuery(id+"F31.imprint","IMPRINT",FACE,{"disambiguationData":[TD([[makeQuery(id+"F31.imprint","IMPRINT",EDGE,{"disambiguationData":[TD([[subQ2,-1.0]])],"derivedFrom":subQ1}),1.0]])]});}
            var Q3;
            {var subQ0=sQuery(id+"F31.wireOp",EDGE,"E127.top");var subQ1=sQuery(id+"F31.wireOp",EDGE,"E126.2.0.0");var subQ2=makeQuery(id+"F31.imprint","INTERSECT",VERTEX,{"derivedFrom":[sQuery(id+"F31.wireOp",EDGE,"E126.1.0.0"),subQ1,subQ0]});Q3=makeQuery(id+"F31.imprint","IMPRINT",FACE,{"disambiguationData":[TD([[makeQuery(id+"F31.imprint","IMPRINT",EDGE,{"disambiguationData":[TD([[subQ2,-1.0]])],"derivedFrom":subQ1}),1.0]])]});}
            var Q4;
            {var subQ0=sQuery(id+"F31.wireOp",EDGE,"E127.top");var subQ1=sQuery(id+"F31.wireOp",EDGE,"E126.3.0.0");var subQ2=makeQuery(id+"F31.imprint","INTERSECT",VERTEX,{"derivedFrom":[sQuery(id+"F31.wireOp",EDGE,"E126.2.0.0"),subQ1,subQ0]});Q4=makeQuery(id+"F31.imprint","IMPRINT",FACE,{"disambiguationData":[TD([[makeQuery(id+"F31.imprint","IMPRINT",EDGE,{"disambiguationData":[TD([[subQ2,-1.0]])],"derivedFrom":subQ1}),1.0]])]});}
            var Q5;
            {var subQ0=sQuery(id+"F31.wireOp",EDGE,"E127.top");var subQ1=sQuery(id+"F31.wireOp",EDGE,"E126.4.0.0");var subQ2=makeQuery(id+"F31.imprint","INTERSECT",VERTEX,{"derivedFrom":[sQuery(id+"F31.wireOp",EDGE,"E126.3.0.0"),subQ1,subQ0]});Q5=makeQuery(id+"F31.imprint","IMPRINT",FACE,{"disambiguationData":[TD([[makeQuery(id+"F31.imprint","IMPRINT",EDGE,{"disambiguationData":[TD([[subQ2,-1.0]])],"derivedFrom":subQ1}),1.0]])]});}
            var Q6;
            {var subQ0=sQuery(id+"F31.wireOp",EDGE,"E127.top");var subQ1=sQuery(id+"F31.wireOp",EDGE,"E126.5.0.0");var subQ2=makeQuery(id+"F31.imprint","INTERSECT",VERTEX,{"derivedFrom":[sQuery(id+"F31.wireOp",EDGE,"E126.4.0.0"),subQ1,subQ0]});Q6=makeQuery(id+"F31.imprint","IMPRINT",FACE,{"disambiguationData":[TD([[makeQuery(id+"F31.imprint","IMPRINT",EDGE,{"disambiguationData":[TD([[subQ2,-1.0]])],"derivedFrom":subQ1}),1.0]])]});}
            var Q7;
            {var subQ0=sQuery(id+"F31.wireOp",EDGE,"E127.top");var subQ1=sQuery(id+"F31.wireOp",EDGE,"E126.6.0.0");var subQ2=makeQuery(id+"F31.imprint","INTERSECT",VERTEX,{"derivedFrom":[sQuery(id+"F31.wireOp",EDGE,"E126.5.0.0"),subQ1,subQ0]});Q7=makeQuery(id+"F31.imprint","IMPRINT",FACE,{"disambiguationData":[TD([[makeQuery(id+"F31.imprint","IMPRINT",EDGE,{"disambiguationData":[TD([[subQ2,-1.0]])],"derivedFrom":subQ1}),1.0]])]});}
            var Q8;
            {var subQ0=sQuery(id+"F31.wireOp",EDGE,"E127.top");var subQ1=sQuery(id+"F31.wireOp",EDGE,"E126.7.0.0");var subQ2=makeQuery(id+"F31.imprint","INTERSECT",VERTEX,{"derivedFrom":[subQ1,subQ0,sQuery(id+"F31.wireOp",EDGE,"E127.right")]});Q8=makeQuery(id+"F31.imprint","IMPRINT",FACE,{"disambiguationData":[TD([[makeQuery(id+"F31.imprint","IMPRINT",EDGE,{"disambiguationData":[TD([[subQ2,1.0]])],"derivedFrom":subQ1}),1.0]])]});}
            var Q9;
            {var subQ0=sQuery(id+"F31.wireOp",EDGE,"E127.top");var subQ1=sQuery(id+"F31.wireOp",EDGE,"E126.7.0.0");var subQ2=makeQuery(id+"F31.imprint","INTERSECT",VERTEX,{"derivedFrom":[subQ1,subQ0,sQuery(id+"F31.wireOp",EDGE,"E127.right")]});Q9=makeQuery(id+"F31.imprint","IMPRINT",FACE,{"disambiguationData":[TD([[makeQuery(id+"F31.imprint","IMPRINT",EDGE,{"disambiguationData":[TD([[subQ2,-1.0]])],"derivedFrom":subQ1}),1.0]])]});}
            var Q10;
            {var subQ0=sQuery(id+"F31.wireOp",EDGE,"E127.top");var subQ1=sQuery(id+"F31.wireOp",EDGE,"E126.6.0.0");var subQ2=makeQuery(id+"F31.imprint","INTERSECT",VERTEX,{"derivedFrom":[sQuery(id+"F31.wireOp",EDGE,"E126.5.0.0"),subQ1,subQ0]});Q10=makeQuery(id+"F31.imprint","IMPRINT",FACE,{"disambiguationData":[TD([[makeQuery(id+"F31.imprint","IMPRINT",EDGE,{"disambiguationData":[TD([[subQ2,1.0]])],"derivedFrom":subQ1}),1.0]])]});}
            var Q11;
            {var subQ0=sQuery(id+"F31.wireOp",EDGE,"E127.top");var subQ1=sQuery(id+"F31.wireOp",EDGE,"E126.5.0.0");var subQ2=makeQuery(id+"F31.imprint","INTERSECT",VERTEX,{"derivedFrom":[sQuery(id+"F31.wireOp",EDGE,"E126.4.0.0"),subQ1,subQ0]});Q11=makeQuery(id+"F31.imprint","IMPRINT",FACE,{"disambiguationData":[TD([[makeQuery(id+"F31.imprint","IMPRINT",EDGE,{"disambiguationData":[TD([[subQ2,1.0]])],"derivedFrom":subQ1}),1.0]])]});}
            var Q12;
            {var subQ0=sQuery(id+"F31.wireOp",EDGE,"E127.top");var subQ1=sQuery(id+"F31.wireOp",EDGE,"E126.4.0.0");var subQ2=makeQuery(id+"F31.imprint","INTERSECT",VERTEX,{"derivedFrom":[sQuery(id+"F31.wireOp",EDGE,"E126.3.0.0"),subQ1,subQ0]});Q12=makeQuery(id+"F31.imprint","IMPRINT",FACE,{"disambiguationData":[TD([[makeQuery(id+"F31.imprint","IMPRINT",EDGE,{"disambiguationData":[TD([[subQ2,1.0]])],"derivedFrom":subQ1}),1.0]])]});}
            var Q13;
            {var subQ0=sQuery(id+"F31.wireOp",EDGE,"E127.top");var subQ1=sQuery(id+"F31.wireOp",EDGE,"E126.3.0.0");var subQ2=makeQuery(id+"F31.imprint","INTERSECT",VERTEX,{"derivedFrom":[sQuery(id+"F31.wireOp",EDGE,"E126.2.0.0"),subQ1,subQ0]});Q13=makeQuery(id+"F31.imprint","IMPRINT",FACE,{"disambiguationData":[TD([[makeQuery(id+"F31.imprint","IMPRINT",EDGE,{"disambiguationData":[TD([[subQ2,1.0]])],"derivedFrom":subQ1}),1.0]])]});}
            var Q14;
            {var subQ0=sQuery(id+"F31.wireOp",EDGE,"E127.top");var subQ1=sQuery(id+"F31.wireOp",EDGE,"E126.2.0.0");var subQ2=makeQuery(id+"F31.imprint","INTERSECT",VERTEX,{"derivedFrom":[sQuery(id+"F31.wireOp",EDGE,"E126.1.0.0"),subQ1,subQ0]});Q14=makeQuery(id+"F31.imprint","IMPRINT",FACE,{"disambiguationData":[TD([[makeQuery(id+"F31.imprint","IMPRINT",EDGE,{"disambiguationData":[TD([[subQ2,1.0]])],"derivedFrom":subQ1}),1.0]])]});}
            var Q15;
            {var subQ0=sQuery(id+"F31.wireOp",EDGE,"E127.top");var subQ1=sQuery(id+"F31.wireOp",EDGE,"E126.1.0.0");var subQ2=makeQuery(id+"F31.imprint","INTERSECT",VERTEX,{"derivedFrom":[sQuery(id+"F31.wireOp",EDGE,"E125"),subQ1,subQ0]});Q15=makeQuery(id+"F31.imprint","IMPRINT",FACE,{"disambiguationData":[TD([[makeQuery(id+"F31.imprint","IMPRINT",EDGE,{"disambiguationData":[TD([[subQ2,1.0]])],"derivedFrom":subQ1}),1.0]])]});}
            var Q16;
            {var subQ0=sQuery(id+"F31.wireOp",EDGE,"E127.top");var subQ1=sQuery(id+"F31.wireOp",EDGE,"E125");var subQ2=makeQuery(id+"F31.imprint","INTERSECT",VERTEX,{"derivedFrom":[subQ1,subQ0,sQuery(id+"F31.wireOp",EDGE,"E127.left")]});Q16=makeQuery(id+"F31.imprint","IMPRINT",FACE,{"disambiguationData":[TD([[makeQuery(id+"F31.imprint","IMPRINT",EDGE,{"disambiguationData":[TD([[subQ2,1.0]])],"derivedFrom":subQ1}),1.0]])]});}
            var Q17;
            Q17=sQuery(id+"F27.wireOp",EDGE,"E102.0");
            var Q18;
            Q18=sQuery(id+"F27.wireOp",EDGE,"E108");
            var Q19;
            Q19=sQuery(id+"F27.wireOp",EDGE,"E121.filletArc");
            var Q20;
            Q20=sQuery(id+"F27.wireOp",EDGE,"E103.0");
            var Q21;
            Q21=sQuery(id+"F27.wireOp",EDGE,"E122.filletArc");
            var Q22;
            Q22=sQuery(id+"F27.wireOp",EDGE,"E106.0");
            var Q23;
            Q23=sQuery(id+"F27.wireOp",EDGE,"E107.0");
            var Q24;
            Q24=sQuery(id+"F27.wireOp",EDGE,"E118");
            sweep(context, id + "F32", {"profiles" : qUnion([Q0, Q1, Q2, Q3, Q4, Q5, Q6, Q7, Q8, Q9, Q10, Q11, Q12, Q13, Q14, Q15, Q16]), "path" : qUnion([Q17, Q18, Q19, Q20, Q21, Q22, Q23, Q24])});
        }
        {
            var Q0;
            Q0=makeQuery(id+"F32.opSweep","SWEPT_BODY",BODY,{"disambiguationData":[OSD([sQuery(id+"F30.wireOp",EDGE,"E123.0"),sQuery(id+"F31.wireOp",EDGE,"E125"),sQuery(id+"F31.wireOp",EDGE,"E126.1.0.0"),sQuery(id+"F31.wireOp",EDGE,"E126.2.0.0"),sQuery(id+"F31.wireOp",EDGE,"E126.3.0.0"),sQuery(id+"F31.wireOp",EDGE,"E126.4.0.0"),sQuery(id+"F31.wireOp",EDGE,"E126.5.0.0"),sQuery(id+"F31.wireOp",EDGE,"E126.6.0.0"),sQuery(id+"F31.wireOp",EDGE,"E126.7.0.0"),sQuery(id+"F31.wireOp",EDGE,"E127.bottom"),sQuery(id+"F31.wireOp",EDGE,"E127.left"),sQuery(id+"F31.wireOp",EDGE,"E127.right")])]});
            var Q1;
            Q1=makeQuery(id+"F21.opExtrude","SWEPT_BODY",BODY,{"disambiguationData":[OSD([sQuery(id+"F20.wireOp",EDGE,"E82.bottom"),sQuery(id+"F20.wireOp",EDGE,"E82.top"),sQuery(id+"F20.wireOp",EDGE,"E82.left"),sQuery(id+"F20.wireOp",EDGE,"E82.right")])]});
            booleanBodies(context, id + "F33", {"operationType" : BooleanOperationType.SUBTRACTION, "tools" : qUnion([Q0]), "targets" : qUnion([Q1])});
        }
        {
            var Q0;
            {var subQ0=sQuery(id+"F31.wireOp",EDGE,"E127.top");var subQ1=sQuery(id+"F31.wireOp",EDGE,"E126.7.0.0");var subQ2=makeQuery(id+"F31.imprint","INTERSECT",VERTEX,{"derivedFrom":[subQ1,subQ0,sQuery(id+"F31.wireOp",EDGE,"E127.right")]});Q0=makeQuery(id+"F31.imprint","IMPRINT",FACE,{"disambiguationData":[TD([[makeQuery(id+"F31.imprint","IMPRINT",EDGE,{"disambiguationData":[TD([[subQ2,-1.0]])],"derivedFrom":subQ1}),1.0]])]});}
            var Q1;
            {var subQ0=sQuery(id+"F31.wireOp",EDGE,"E127.top");var subQ1=sQuery(id+"F31.wireOp",EDGE,"E126.7.0.0");var subQ2=makeQuery(id+"F31.imprint","INTERSECT",VERTEX,{"derivedFrom":[subQ1,subQ0,sQuery(id+"F31.wireOp",EDGE,"E127.right")]});Q1=makeQuery(id+"F31.imprint","IMPRINT",FACE,{"disambiguationData":[TD([[makeQuery(id+"F31.imprint","IMPRINT",EDGE,{"disambiguationData":[TD([[subQ2,1.0]])],"derivedFrom":subQ1}),1.0]])]});}
            var Q2;
            {var subQ0=sQuery(id+"F31.wireOp",EDGE,"E127.top");var subQ1=sQuery(id+"F31.wireOp",EDGE,"E126.6.0.0");var subQ2=makeQuery(id+"F31.imprint","INTERSECT",VERTEX,{"derivedFrom":[sQuery(id+"F31.wireOp",EDGE,"E126.5.0.0"),subQ1,subQ0]});Q2=makeQuery(id+"F31.imprint","IMPRINT",FACE,{"disambiguationData":[TD([[makeQuery(id+"F31.imprint","IMPRINT",EDGE,{"disambiguationData":[TD([[subQ2,-1.0]])],"derivedFrom":subQ1}),1.0]])]});}
            var Q3;
            {var subQ0=sQuery(id+"F31.wireOp",EDGE,"E127.top");var subQ1=sQuery(id+"F31.wireOp",EDGE,"E126.6.0.0");var subQ2=makeQuery(id+"F31.imprint","INTERSECT",VERTEX,{"derivedFrom":[sQuery(id+"F31.wireOp",EDGE,"E126.5.0.0"),subQ1,subQ0]});Q3=makeQuery(id+"F31.imprint","IMPRINT",FACE,{"disambiguationData":[TD([[makeQuery(id+"F31.imprint","IMPRINT",EDGE,{"disambiguationData":[TD([[subQ2,1.0]])],"derivedFrom":subQ1}),1.0]])]});}
            var Q4;
            {var subQ0=sQuery(id+"F31.wireOp",EDGE,"E127.top");var subQ1=sQuery(id+"F31.wireOp",EDGE,"E126.5.0.0");var subQ2=makeQuery(id+"F31.imprint","INTERSECT",VERTEX,{"derivedFrom":[sQuery(id+"F31.wireOp",EDGE,"E126.4.0.0"),subQ1,subQ0]});Q4=makeQuery(id+"F31.imprint","IMPRINT",FACE,{"disambiguationData":[TD([[makeQuery(id+"F31.imprint","IMPRINT",EDGE,{"disambiguationData":[TD([[subQ2,-1.0]])],"derivedFrom":subQ1}),1.0]])]});}
            var Q5;
            {var subQ0=sQuery(id+"F31.wireOp",EDGE,"E127.top");var subQ1=sQuery(id+"F31.wireOp",EDGE,"E126.5.0.0");var subQ2=makeQuery(id+"F31.imprint","INTERSECT",VERTEX,{"derivedFrom":[sQuery(id+"F31.wireOp",EDGE,"E126.4.0.0"),subQ1,subQ0]});Q5=makeQuery(id+"F31.imprint","IMPRINT",FACE,{"disambiguationData":[TD([[makeQuery(id+"F31.imprint","IMPRINT",EDGE,{"disambiguationData":[TD([[subQ2,1.0]])],"derivedFrom":subQ1}),1.0]])]});}
            var Q6;
            {var subQ0=sQuery(id+"F31.wireOp",EDGE,"E127.top");var subQ1=sQuery(id+"F31.wireOp",EDGE,"E126.4.0.0");var subQ2=makeQuery(id+"F31.imprint","INTERSECT",VERTEX,{"derivedFrom":[sQuery(id+"F31.wireOp",EDGE,"E126.3.0.0"),subQ1,subQ0]});Q6=makeQuery(id+"F31.imprint","IMPRINT",FACE,{"disambiguationData":[TD([[makeQuery(id+"F31.imprint","IMPRINT",EDGE,{"disambiguationData":[TD([[subQ2,-1.0]])],"derivedFrom":subQ1}),1.0]])]});}
            var Q7;
            {var subQ0=sQuery(id+"F31.wireOp",EDGE,"E127.top");var subQ1=sQuery(id+"F31.wireOp",EDGE,"E126.4.0.0");var subQ2=makeQuery(id+"F31.imprint","INTERSECT",VERTEX,{"derivedFrom":[sQuery(id+"F31.wireOp",EDGE,"E126.3.0.0"),subQ1,subQ0]});Q7=makeQuery(id+"F31.imprint","IMPRINT",FACE,{"disambiguationData":[TD([[makeQuery(id+"F31.imprint","IMPRINT",EDGE,{"disambiguationData":[TD([[subQ2,1.0]])],"derivedFrom":subQ1}),1.0]])]});}
            var Q8;
            {var subQ0=sQuery(id+"F31.wireOp",EDGE,"E127.top");var subQ1=sQuery(id+"F31.wireOp",EDGE,"E126.3.0.0");var subQ2=makeQuery(id+"F31.imprint","INTERSECT",VERTEX,{"derivedFrom":[sQuery(id+"F31.wireOp",EDGE,"E126.2.0.0"),subQ1,subQ0]});Q8=makeQuery(id+"F31.imprint","IMPRINT",FACE,{"disambiguationData":[TD([[makeQuery(id+"F31.imprint","IMPRINT",EDGE,{"disambiguationData":[TD([[subQ2,-1.0]])],"derivedFrom":subQ1}),1.0]])]});}
            var Q9;
            {var subQ0=sQuery(id+"F31.wireOp",EDGE,"E127.top");var subQ1=sQuery(id+"F31.wireOp",EDGE,"E126.3.0.0");var subQ2=makeQuery(id+"F31.imprint","INTERSECT",VERTEX,{"derivedFrom":[sQuery(id+"F31.wireOp",EDGE,"E126.2.0.0"),subQ1,subQ0]});Q9=makeQuery(id+"F31.imprint","IMPRINT",FACE,{"disambiguationData":[TD([[makeQuery(id+"F31.imprint","IMPRINT",EDGE,{"disambiguationData":[TD([[subQ2,1.0]])],"derivedFrom":subQ1}),1.0]])]});}
            var Q10;
            {var subQ0=sQuery(id+"F31.wireOp",EDGE,"E127.top");var subQ1=sQuery(id+"F31.wireOp",EDGE,"E126.2.0.0");var subQ2=makeQuery(id+"F31.imprint","INTERSECT",VERTEX,{"derivedFrom":[sQuery(id+"F31.wireOp",EDGE,"E126.1.0.0"),subQ1,subQ0]});Q10=makeQuery(id+"F31.imprint","IMPRINT",FACE,{"disambiguationData":[TD([[makeQuery(id+"F31.imprint","IMPRINT",EDGE,{"disambiguationData":[TD([[subQ2,-1.0]])],"derivedFrom":subQ1}),1.0]])]});}
            var Q11;
            {var subQ0=sQuery(id+"F31.wireOp",EDGE,"E127.top");var subQ1=sQuery(id+"F31.wireOp",EDGE,"E126.2.0.0");var subQ2=makeQuery(id+"F31.imprint","INTERSECT",VERTEX,{"derivedFrom":[sQuery(id+"F31.wireOp",EDGE,"E126.1.0.0"),subQ1,subQ0]});Q11=makeQuery(id+"F31.imprint","IMPRINT",FACE,{"disambiguationData":[TD([[makeQuery(id+"F31.imprint","IMPRINT",EDGE,{"disambiguationData":[TD([[subQ2,1.0]])],"derivedFrom":subQ1}),1.0]])]});}
            var Q12;
            {var subQ0=sQuery(id+"F31.wireOp",EDGE,"E127.top");var subQ1=sQuery(id+"F31.wireOp",EDGE,"E126.1.0.0");var subQ2=makeQuery(id+"F31.imprint","INTERSECT",VERTEX,{"derivedFrom":[sQuery(id+"F31.wireOp",EDGE,"E125"),subQ1,subQ0]});Q12=makeQuery(id+"F31.imprint","IMPRINT",FACE,{"disambiguationData":[TD([[makeQuery(id+"F31.imprint","IMPRINT",EDGE,{"disambiguationData":[TD([[subQ2,-1.0]])],"derivedFrom":subQ1}),1.0]])]});}
            var Q13;
            {var subQ0=sQuery(id+"F31.wireOp",EDGE,"E127.top");var subQ1=sQuery(id+"F31.wireOp",EDGE,"E126.1.0.0");var subQ2=makeQuery(id+"F31.imprint","INTERSECT",VERTEX,{"derivedFrom":[sQuery(id+"F31.wireOp",EDGE,"E125"),subQ1,subQ0]});Q13=makeQuery(id+"F31.imprint","IMPRINT",FACE,{"disambiguationData":[TD([[makeQuery(id+"F31.imprint","IMPRINT",EDGE,{"disambiguationData":[TD([[subQ2,1.0]])],"derivedFrom":subQ1}),1.0]])]});}
            var Q14;
            {var subQ0=sQuery(id+"F31.wireOp",EDGE,"E127.top");var subQ1=sQuery(id+"F31.wireOp",EDGE,"E125");var subQ2=makeQuery(id+"F31.imprint","INTERSECT",VERTEX,{"derivedFrom":[subQ1,subQ0,sQuery(id+"F31.wireOp",EDGE,"E127.left")]});Q14=makeQuery(id+"F31.imprint","IMPRINT",FACE,{"disambiguationData":[TD([[makeQuery(id+"F31.imprint","IMPRINT",EDGE,{"disambiguationData":[TD([[subQ2,-1.0]])],"derivedFrom":subQ1}),1.0]])]});}
            var Q15;
            {var subQ0=sQuery(id+"F31.wireOp",EDGE,"E127.top");var subQ1=sQuery(id+"F31.wireOp",EDGE,"E125");var subQ2=makeQuery(id+"F31.imprint","INTERSECT",VERTEX,{"derivedFrom":[subQ1,subQ0,sQuery(id+"F31.wireOp",EDGE,"E127.left")]});Q15=makeQuery(id+"F31.imprint","IMPRINT",FACE,{"disambiguationData":[TD([[makeQuery(id+"F31.imprint","IMPRINT",EDGE,{"disambiguationData":[TD([[subQ2,1.0]])],"derivedFrom":subQ1}),1.0]])]});}
            var Q16;
            Q16=sQuery(id+"F27.wireOp",EDGE,"E102.0");
            var Q17;
            Q17=sQuery(id+"F27.wireOp",EDGE,"E121.filletArc");
            var Q18;
            Q18=sQuery(id+"F27.wireOp",EDGE,"E107.0");
            var Q19;
            Q19=sQuery(id+"F27.wireOp",EDGE,"E122.filletArc");
            var Q20;
            Q20=sQuery(id+"F27.wireOp",EDGE,"E106.0");
            var Q21;
            Q21=sQuery(id+"F27.wireOp",EDGE,"E103.0");
            sweep(context, id + "F34", {"profiles" : qUnion([Q0, Q1, Q2, Q3, Q4, Q5, Q6, Q7, Q8, Q9, Q10, Q11, Q12, Q13, Q14, Q15]), "path" : qUnion([Q16, Q17, Q18, Q19, Q20, Q21])});
        }
        {
            var Q0;
            Q0=qCreatedBy(id+"F3.planeOp",FACE);
            var sketch = newSketch(context, id + "F35", { "sketchPlane" : qUnion([Q0])});
            skLineSegment(sketch, "E129", {"start": v(0, 0) * mm, "end": v(0, -31.75) * mm});
            skLineSegment(sketch, "E130.bottom", {"start": v(0, -31.75) * mm, "end": v(164.62, -31.75) * mm});
            skLineSegment(sketch, "E130.top", {"start": v(0, -38.1) * mm, "end": v(164.62, -38.1) * mm});
            skLineSegment(sketch, "E130.left", {"start": v(0, -31.75) * mm, "end": v(0, -38.1) * mm});
            skLineSegment(sketch, "E130.right", {"start": v(164.62, -31.75) * mm, "end": v(164.62, -38.1) * mm});
            skSolve(sketch);
        }
        {
            var Q0;
            Q0=makeQuery(id+"F35.imprint","IMPRINT",FACE,{"disambiguationData":[TD([[makeQuery(id+"F35.imprint","IMPRINT",EDGE,{"derivedFrom":sQuery(id+"F35.wireOp",EDGE,"E130.bottom")}),-1.0]])]});
            extrude(context, id + "F36", {"entities" : qUnion([Q0]), "oppositeDirection" : true, "depth" : 88.9 * mm});
        }
        {
            var Q0;
            Q0=makeQuery(id+"F36.opExtrude","SWEPT_BODY",BODY,{"disambiguationData":[OSD([sQuery(id+"F35.wireOp",EDGE,"E130.bottom"),sQuery(id+"F35.wireOp",EDGE,"E130.top"),sQuery(id+"F35.wireOp",EDGE,"E130.left"),sQuery(id+"F35.wireOp",EDGE,"E130.right")])]});
            var Q1;
            Q1=makeQuery(id+"F9.opExtrude","SWEPT_BODY",BODY,{"disambiguationData":[OSD([sQuery(id+"F6.wireOp",EDGE,"E0"),sQuery(id+"F6.wireOp",EDGE,"E12"),sQuery(id+"F6.wireOp",EDGE,"E13"),sQuery(id+"F6.wireOp",EDGE,"E14")])]});
            var Q2;
            Q2=makeQuery(id+"F7.opExtrude","SWEPT_BODY",BODY,{"disambiguationData":[OSD([sQuery(id+"F6.wireOp",EDGE,"E2"),sQuery(id+"F6.wireOp",EDGE,"E3"),sQuery(id+"F6.wireOp",EDGE,"E4"),sQuery(id+"F6.wireOp",EDGE,"E12"),sQuery(id+"F6.wireOp",EDGE,"E13"),sQuery(id+"F6.wireOp",EDGE,"E14"),sQuery(id+"F6.wireOp",EDGE,"E15"),sQuery(id+"F6.wireOp",EDGE,"E16"),sQuery(id+"F6.wireOp",EDGE,"E17"),sQuery(id+"F6.wireOp",EDGE,"E18")])]});
            var Q3;
            Q3=makeQuery(id+"F10.opExtrude","SWEPT_BODY",BODY,{"disambiguationData":[OSD([sQuery(id+"F6.wireOp",EDGE,"E4"),sQuery(id+"F6.wireOp",EDGE,"E6"),sQuery(id+"F6.wireOp",EDGE,"E8"),sQuery(id+"F6.wireOp",EDGE,"E9"),sQuery(id+"F6.wireOp",EDGE,"E10"),sQuery(id+"F6.wireOp",EDGE,"E11")])]});
            booleanBodies(context, id + "F37", {"operationType" : BooleanOperationType.SUBTRACTION, "tools" : qUnion([Q0]), "targets" : qUnion([Q1, Q2, Q3])});
        }
        {
            var Q0;
            Q0=qCreatedBy(id+"F4.planeOp",FACE);
            var sketch = newSketch(context, id + "F38", { "sketchPlane" : qUnion([Q0])});
            skCircle(sketch, "E131", {"center": v(0, 107.95) * mm, "radius": 41.28 * mm});
            skLineSegment(sketch, "E132", {"start": v(0, 0) * mm, "end": v(0, 107.95) * mm});
            skSolve(sketch);
        }
        {
            var Q0;
            Q0=qCreatedBy(id+"F5.planeOp",FACE);
            var sketch = newSketch(context, id + "F39", { "sketchPlane" : qUnion([Q0])});
            skLineSegment(sketch, "E133", {"start": v(0, 0) * mm, "end": v(0, 107.95) * mm});
            skCircle(sketch, "E134", {"center": v(0, 107.95) * mm, "radius": 44.45 * mm});
            skSolve(sketch);
        }
        {
            var Q0;
            Q0=makeQuery(id+"F39.imprint","IMPRINT",FACE,{"disambiguationData":[TD([[makeQuery(id+"F39.imprint","IMPRINT",EDGE,{"derivedFrom":sQuery(id+"F39.wireOp",EDGE,"E134")}),1.0]])]});
            var Q1;
            Q1=makeQuery(id+"F38.imprint","IMPRINT",FACE,{"disambiguationData":[TD([[makeQuery(id+"F38.imprint","IMPRINT",EDGE,{"derivedFrom":sQuery(id+"F38.wireOp",EDGE,"E131")}),1.0]])]});
            loft(context, id + "F40", {"sheetProfilesArray" : [{ "sheetProfileEntities" : qUnion([Q0]) }, { "sheetProfileEntities" : qUnion([Q1]) }]});
        }
        {
            var Q0;
            Q0=qCreatedBy(id+"F3.planeOp",FACE);
            var sketch = newSketch(context, id + "F41", { "sketchPlane" : qUnion([Q0])});
            skLineSegment(sketch, "E135", {"start": v(0, 0) * mm, "end": v(107.95, 0) * mm});
            skLineSegment(sketch, "E136", {"start": v(107.95, 0) * mm, "end": v(107.95, 3.18) * mm});
            skCircle(sketch, "E137", {"center": v(107.95, 3.18) * mm, "radius": 33.34 * mm});
            skSolve(sketch);
        }
        {
            var Q0;
            Q0=makeQuery(id+"F29.opExtrude","SWEPT_BODY",BODY,{"disambiguationData":[OSD([sQuery(id+"F27.wireOp",EDGE,"E93"),sQuery(id+"F27.wireOp",EDGE,"E97"),sQuery(id+"F27.wireOp",EDGE,"E108"),sQuery(id+"F27.wireOp",EDGE,"E109"),sQuery(id+"F27.wireOp",EDGE,"E111"),sQuery(id+"F27.wireOp",EDGE,"E112"),sQuery(id+"F27.wireOp",EDGE,"E113"),sQuery(id+"F27.wireOp",EDGE,"E114"),sQuery(id+"F27.wireOp",EDGE,"E117"),sQuery(id+"F27.wireOp",EDGE,"E118"),sQuery(id+"F27.wireOp",EDGE,"E119"),sQuery(id+"F27.wireOp",EDGE,"E120")])]});
            deleteBodies(context, id + "F42", {"entities" : qUnion([Q0])});
        }
        {
            var Q0;
            Q0=makeQuery(id+"F41.imprint","IMPRINT",FACE,{"disambiguationData":[TD([[makeQuery(id+"F41.imprint","IMPRINT",EDGE,{"derivedFrom":sQuery(id+"F41.wireOp",EDGE,"E137")}),1.0]])]});
            extrude(context, id + "F43", {"entities" : qUnion([Q0]), "depth" : 4.76 * mm});
        }
        {
            var Q0;
            Q0=makeQuery(id+"F14.boolean.opBoolean","COPY",FACE,{"derivedFrom":makeQuery(id+"F14.opExtrude","SWEPT_FACE",FACE,{"disambiguationData":[OSD([sQuery(id+"F13.wireOp",EDGE,"E45.0")])]})});
            var sketch = newSketch(context, id + "F44", { "sketchPlane" : qUnion([Q0])});
            skLineSegment(sketch, "E138.bottom", {"start": v(-16.5, -6.72) * mm, "end": v(-1.27, -6.72) * mm});
            skLineSegment(sketch, "E138.top", {"start": v(-16.5, -60.6) * mm, "end": v(-8.89, -60.6) * mm});
            skLineSegment(sketch, "E138.left", {"start": v(-16.5, -6.72) * mm, "end": v(-16.5, -23.18) * mm});
            skLineSegment(sketch, "E138.right", {"start": v(16.5, -6.72) * mm, "end": v(16.5, -23.18) * mm});
            skLineSegment(sketch, "E139", {"start": v(-16.51, -23.18) * mm, "end": v(-1.27, -23.18) * mm});
            skLineSegment(sketch, "E140.0", {"start": v(1.27, -6.72) * mm, "end": v(1.27, -23.18) * mm});
            skLineSegment(sketch, "E141.0", {"start": v(-1.27, -6.72) * mm, "end": v(-1.27, -23.18) * mm});
            skLineSegment(sketch, "E142", {"start": v(-16.5, -69.9) * mm, "end": v(-1.27, -69.9) * mm});
            skLineSegment(sketch, "E143", {"start": v(-8.89, -69.9) * mm, "end": v(-8.89, -60.6) * mm});
            skLineSegment(sketch, "E144", {"start": v(-8.9, -60.6) * mm, "end": v(-1.27, -52.98) * mm});
            skLineSegment(sketch, "E145.MirrorCS", {"start": v(8.89, -60.6) * mm, "end": v(1.27, -52.98) * mm});
            skCircle(sketch, "E146", {"center": v(0, -57.19) * mm, "radius": 2.54 * mm});
            skPoint(sketch, "E147.orphan", {"position": v(-8.96, -42.74) * mm});
            skPoint(sketch, "E148.orphan", {"position": v(8.96, -42.74) * mm});
            skPoint(sketch, "E149.orphan", {"position": v(0, -60.6) * mm});
            skLineSegment(sketch, "E150", {"start": v(-16.5, -44.72) * mm, "end": v(-1.27, -44.72) * mm});
            skLineSegment(sketch, "E151.trimOffspring", {"start": v(-16.5, -44.72) * mm, "end": v(-16.51, -60.6) * mm});
            skLineSegment(sketch, "E152.trimOffspring", {"start": v(16.5, -44.72) * mm, "end": v(16.5, -60.6) * mm});
            skLineSegment(sketch, "E153.trimOffspring", {"start": v(-1.27, -44.72) * mm, "end": v(-1.27, -52.98) * mm});
            skLineSegment(sketch, "E154.trimOffspring", {"start": v(1.27, -44.72) * mm, "end": v(1.27, -52.98) * mm});
            skLineSegment(sketch, "E155.trimOffspring", {"start": v(1.27, -44.72) * mm, "end": v(16.5, -44.72) * mm});
            skLineSegment(sketch, "E156.trimOffspring", {"start": v(1.27, -23.18) * mm, "end": v(16.5, -23.18) * mm});
            skLineSegment(sketch, "E157.trimOffspring", {"start": v(1.27, -6.72) * mm, "end": v(16.5, -6.72) * mm});
            skLineSegment(sketch, "E158.0", {"start": v(-15.06, -22.54) * mm, "end": v(-10.98, -18.14) * mm});
            skLineSegment(sketch, "E159.0", {"start": v(25.4, 2.17) * mm, "end": v(-25.4, 2.17) * mm});
            skLineSegment(sketch, "E159.1", {"start": v(25.4, -69.49) * mm, "end": v(25.4, 2.17) * mm});
            skLineSegment(sketch, "E159.2", {"start": v(-25.4, -69.49) * mm, "end": v(25.4, -69.49) * mm});
            skLineSegment(sketch, "E159.3", {"start": v(-25.4, 2.17) * mm, "end": v(-25.4, -69.49) * mm});
            skLineSegment(sketch, "E160.0", {"start": v(-15.87, -21.56) * mm, "end": v(-11.9, -17.27) * mm});
            skLineSegment(sketch, "E161.0", {"start": v(-15.06, -7.35) * mm, "end": v(-10.98, -11.76) * mm});
            skLineSegment(sketch, "E162.0", {"start": v(-15.88, -8.34) * mm, "end": v(-11.9, -12.62) * mm});
            skArc(sketch, "E163", {"start": v(-11.9, -12.62) * mm, "mid": v(-12.7, -14.95) * mm, "end": v(-11.9, -17.27) * mm});
            skLineSegment(sketch, "E164.trimOffspring", {"start": v(-15.06, -7.35) * mm, "end": v(-2.72, -7.35) * mm});
            skLineSegment(sketch, "E165.trimOffspring", {"start": v(-15.88, -8.34) * mm, "end": v(-15.87, -21.56) * mm});
            skLineSegment(sketch, "E166.trimOffspring", {"start": v(-6.8, -11.76) * mm, "end": v(-2.72, -7.35) * mm});
            skLineSegment(sketch, "E167.trimOffspring", {"start": v(-5.87, -12.62) * mm, "end": v(-1.9, -8.34) * mm});
            skArc(sketch, "E168.trimOffspring", {"start": v(-6.8, -11.76) * mm, "mid": v(-8.9, -11.14) * mm, "end": v(-10.98, -11.76) * mm});
            skLineSegment(sketch, "E169.trimOffspring", {"start": v(-15.06, -22.54) * mm, "end": v(-2.72, -22.54) * mm});
            skLineSegment(sketch, "E170.trimOffspring", {"start": v(-1.9, -8.34) * mm, "end": v(-1.9, -21.56) * mm});
            skArc(sketch, "E171.trimOffspring", {"start": v(-10.98, -18.14) * mm, "mid": v(-8.89, -18.76) * mm, "end": v(-6.8, -18.14) * mm});
            skLineSegment(sketch, "E172.trimOffspring", {"start": v(-6.8, -18.14) * mm, "end": v(-2.72, -22.54) * mm});
            skLineSegment(sketch, "E173.trimOffspring", {"start": v(-5.87, -17.27) * mm, "end": v(-1.9, -21.56) * mm});
            skCircle(sketch, "E174", {"center": v(-8.9, -14.95) * mm, "radius": 2.54 * mm});
            skLineSegment(sketch, "E175.MirrorCS", {"start": v(5.87, -17.27) * mm, "end": v(1.9, -21.56) * mm});
            skLineSegment(sketch, "E176.MirrorCS", {"start": v(15.06, -7.35) * mm, "end": v(2.72, -7.35) * mm});
            skLineSegment(sketch, "E177.MirrorCS", {"start": v(15.06, -22.54) * mm, "end": v(2.72, -22.54) * mm});
            skLineSegment(sketch, "E178.MirrorCS", {"start": v(15.88, -8.34) * mm, "end": v(15.87, -21.56) * mm});
            skLineSegment(sketch, "E179.MirrorCS", {"start": v(6.8, -11.76) * mm, "end": v(2.72, -7.35) * mm});
            skLineSegment(sketch, "E180.MirrorCS", {"start": v(15.88, -8.34) * mm, "end": v(11.9, -12.62) * mm});
            skLineSegment(sketch, "E181.MirrorCS", {"start": v(1.9, -8.34) * mm, "end": v(1.9, -21.56) * mm});
            skLineSegment(sketch, "E182.MirrorCS", {"start": v(15.06, -22.54) * mm, "end": v(10.98, -18.14) * mm});
            skArc(sketch, "E183.MirrorCS", {"start": v(6.8, -11.76) * mm, "mid": v(8.89, -11.14) * mm, "end": v(10.98, -11.76) * mm});
            skLineSegment(sketch, "E184.MirrorCS", {"start": v(6.8, -18.14) * mm, "end": v(2.72, -22.54) * mm});
            skArc(sketch, "E185.MirrorCS", {"start": v(11.9, -12.62) * mm, "mid": v(12.7, -14.95) * mm, "end": v(11.9, -17.27) * mm});
            skLineSegment(sketch, "E186.MirrorCS", {"start": v(15.06, -7.35) * mm, "end": v(10.98, -11.76) * mm});
            skLineSegment(sketch, "E187.MirrorCS", {"start": v(15.87, -21.56) * mm, "end": v(11.9, -17.27) * mm});
            skLineSegment(sketch, "E188.MirrorCS", {"start": v(5.87, -12.62) * mm, "end": v(1.9, -8.34) * mm});
            skCircle(sketch, "E189.MirrorC", {"center": v(8.9, -14.95) * mm, "radius": 2.54 * mm});
            skArc(sketch, "E190.MirrorCS", {"start": v(10.98, -18.14) * mm, "mid": v(8.89, -18.76) * mm, "end": v(6.8, -18.14) * mm});
            skLineSegment(sketch, "E191.MirrorCS", {"start": v(-16.5, -42.18) * mm, "end": v(-1.27, -42.18) * mm});
            skLineSegment(sketch, "E192.MirrorCS", {"start": v(-16.5, -42.18) * mm, "end": v(-16.5, -25.72) * mm});
            skLineSegment(sketch, "E193.MirrorCS", {"start": v(-5.87, -36.27) * mm, "end": v(-1.9, -40.56) * mm});
            skArc(sketch, "E194.MirrorCS", {"start": v(-10.98, -30.76) * mm, "mid": v(-8.89, -30.14) * mm, "end": v(-6.8, -30.76) * mm});
            skLineSegment(sketch, "E195.MirrorCS", {"start": v(-15.06, -26.35) * mm, "end": v(-10.98, -30.76) * mm});
            skLineSegment(sketch, "E196.MirrorCS", {"start": v(5.87, -31.62) * mm, "end": v(1.9, -27.34) * mm});
            skLineSegment(sketch, "E197.MirrorCS", {"start": v(15.87, -27.34) * mm, "end": v(11.9, -31.62) * mm});
            skArc(sketch, "E198.MirrorCS", {"start": v(-11.9, -36.27) * mm, "mid": v(-12.7, -33.95) * mm, "end": v(-11.9, -31.62) * mm});
            skLineSegment(sketch, "E199.MirrorCS", {"start": v(15.06, -41.54) * mm, "end": v(10.98, -37.14) * mm});
            skArc(sketch, "E200.MirrorCS", {"start": v(11.9, -36.27) * mm, "mid": v(12.7, -33.95) * mm, "end": v(11.9, -31.62) * mm});
            skLineSegment(sketch, "E201.MirrorCS", {"start": v(-15.88, -40.56) * mm, "end": v(-11.9, -36.27) * mm});
            skLineSegment(sketch, "E202.MirrorCS", {"start": v(15.88, -40.56) * mm, "end": v(11.9, -36.27) * mm});
            skLineSegment(sketch, "E203.MirrorCS", {"start": v(-15.06, -26.35) * mm, "end": v(-2.72, -26.35) * mm});
            skArc(sketch, "E204.MirrorCS", {"start": v(10.98, -30.76) * mm, "mid": v(8.89, -30.14) * mm, "end": v(6.8, -30.76) * mm});
            skLineSegment(sketch, "E205.MirrorCS", {"start": v(1.27, -42.18) * mm, "end": v(16.5, -42.18) * mm});
            skCircle(sketch, "E206.MirrorC", {"center": v(-8.9, -33.95) * mm, "radius": 2.54 * mm});
            skLineSegment(sketch, "E207.MirrorCS", {"start": v(-6.8, -37.14) * mm, "end": v(-2.72, -41.54) * mm});
            skLineSegment(sketch, "E208.MirrorCS", {"start": v(-15.87, -27.34) * mm, "end": v(-11.9, -31.62) * mm});
            skLineSegment(sketch, "E209.MirrorCS", {"start": v(-6.8, -30.76) * mm, "end": v(-2.72, -26.35) * mm});
            skLineSegment(sketch, "E210.MirrorCS", {"start": v(1.27, -42.18) * mm, "end": v(1.27, -25.72) * mm});
            skLineSegment(sketch, "E211.MirrorCS", {"start": v(15.06, -26.35) * mm, "end": v(10.98, -30.76) * mm});
            skLineSegment(sketch, "E212.MirrorCS", {"start": v(16.51, -42.18) * mm, "end": v(16.5, -25.72) * mm});
            skLineSegment(sketch, "E213.MirrorCS", {"start": v(6.8, -30.76) * mm, "end": v(2.72, -26.35) * mm});
            skLineSegment(sketch, "E214.MirrorCS", {"start": v(5.87, -36.27) * mm, "end": v(1.9, -40.56) * mm});
            skLineSegment(sketch, "E215.MirrorCS", {"start": v(-15.88, -40.56) * mm, "end": v(-15.87, -27.34) * mm});
            skLineSegment(sketch, "E216.MirrorCS", {"start": v(-5.87, -31.62) * mm, "end": v(-1.9, -27.34) * mm});
            skLineSegment(sketch, "E217.MirrorCS", {"start": v(-16.51, -25.72) * mm, "end": v(-1.27, -25.72) * mm});
            skLineSegment(sketch, "E218.MirrorCS", {"start": v(6.8, -37.14) * mm, "end": v(2.72, -41.54) * mm});
            skCircle(sketch, "E219.MirrorC", {"center": v(8.9, -33.95) * mm, "radius": 2.54 * mm});
            skArc(sketch, "E220.MirrorCS", {"start": v(-6.8, -37.14) * mm, "mid": v(-8.89, -37.76) * mm, "end": v(-10.98, -37.14) * mm});
            skLineSegment(sketch, "E221.MirrorCS", {"start": v(-15.06, -41.54) * mm, "end": v(-10.98, -37.14) * mm});
            skLineSegment(sketch, "E222.MirrorCS", {"start": v(1.27, -25.72) * mm, "end": v(16.5, -25.72) * mm});
            skLineSegment(sketch, "E223.MirrorCS", {"start": v(-15.06, -41.54) * mm, "end": v(-2.72, -41.54) * mm});
            skLineSegment(sketch, "E224.MirrorCS", {"start": v(15.06, -26.35) * mm, "end": v(2.72, -26.35) * mm});
            skLineSegment(sketch, "E225.MirrorCS", {"start": v(-1.9, -40.56) * mm, "end": v(-1.9, -27.34) * mm});
            skLineSegment(sketch, "E226.MirrorCS", {"start": v(15.06, -41.54) * mm, "end": v(2.72, -41.54) * mm});
            skLineSegment(sketch, "E227.MirrorCS", {"start": v(1.9, -40.56) * mm, "end": v(1.9, -27.34) * mm});
            skArc(sketch, "E228.MirrorCS", {"start": v(6.8, -37.14) * mm, "mid": v(8.89, -37.76) * mm, "end": v(10.98, -37.14) * mm});
            skLineSegment(sketch, "E229.MirrorCS", {"start": v(-1.27, -42.18) * mm, "end": v(-1.27, -25.72) * mm});
            skLineSegment(sketch, "E230.MirrorCS", {"start": v(15.88, -40.56) * mm, "end": v(15.87, -27.34) * mm});
            skLineSegment(sketch, "E231.trimOffspring", {"start": v(8.89, -60.6) * mm, "end": v(16.5, -60.6) * mm});
            skLineSegment(sketch, "E232.0", {"start": v(-15.87, -59.33) * mm, "end": v(-14.99, -59.33) * mm});
            skLineSegment(sketch, "E233.0", {"start": v(-2.54, -45.99) * mm, "end": v(-2.54, -52.45) * mm});
            skLineSegment(sketch, "E234.1.0.0", {"start": v(-13.97, -45.99) * mm, "end": v(-13.97, -59.33) * mm});
            skLineSegment(sketch, "E234.2.0.0", {"start": v(-12.7, -45.99) * mm, "end": v(-12.7, -59.33) * mm});
            skLineSegment(sketch, "E234.3.0.0", {"start": v(-11.43, -45.99) * mm, "end": v(-11.43, -59.33) * mm});
            skLineSegment(sketch, "E234.4.0.0", {"start": v(-10.16, -45.99) * mm, "end": v(-10.16, -59.33) * mm});
            skLineSegment(sketch, "E234.5.0.0", {"start": v(-8.89, -45.99) * mm, "end": v(-8.89, -57.53) * mm});
            skLineSegment(sketch, "E234.6.0.0", {"start": v(-7.62, -45.99) * mm, "end": v(-7.62, -57.53) * mm});
            skLineSegment(sketch, "E234.7.0.0", {"start": v(-6.35, -45.99) * mm, "end": v(-6.35, -54.99) * mm});
            skLineSegment(sketch, "E234.8.0.0", {"start": v(-5.08, -45.99) * mm, "end": v(-5.08, -54.99) * mm});
            skLineSegment(sketch, "E234.9.0.0", {"start": v(-3.8, -45.99) * mm, "end": v(-3.8, -52.45) * mm});
            skLineSegment(sketch, "E234.direction1", {"start": v(-15.24, -60.6) * mm, "end": v(-13.97, -60.6) * mm, "construction": true});
            skPoint(sketch, "E235.orphan", {"position": v(-15.24, -44.72) * mm});
            skPoint(sketch, "E236.orphan", {"position": v(-13.97, -44.72) * mm});
            skPoint(sketch, "E237.orphan", {"position": v(-12.7, -44.72) * mm});
            skPoint(sketch, "E238.orphan", {"position": v(-11.43, -44.72) * mm});
            skPoint(sketch, "E239.orphan", {"position": v(-10.16, -44.72) * mm});
            skPoint(sketch, "E240.orphan", {"position": v(-8.89, -44.72) * mm});
            skPoint(sketch, "E241.orphan", {"position": v(-7.62, -44.72) * mm});
            skPoint(sketch, "E242.orphan", {"position": v(-6.35, -44.72) * mm});
            skPoint(sketch, "E243.orphan", {"position": v(-5.08, -44.72) * mm});
            skPoint(sketch, "E244.orphan", {"position": v(-3.8, -44.72) * mm});
            skPoint(sketch, "E245.orphan", {"position": v(-12.7, -60.6) * mm});
            skPoint(sketch, "E246.orphan", {"position": v(-11.43, -60.6) * mm});
            skPoint(sketch, "E247.orphan", {"position": v(-10.16, -60.6) * mm});
            skPoint(sketch, "E248.orphan", {"position": v(-7.62, -60.6) * mm});
            skPoint(sketch, "E249.orphan", {"position": v(-6.35, -60.6) * mm});
            skPoint(sketch, "E250.orphan", {"position": v(-5.08, -60.6) * mm});
            skArc(sketch, "E251", {"start": v(-2.54, -45.99) * mm, "mid": v(-3.17, -45.35) * mm, "end": v(-3.8, -45.99) * mm});
            skPoint(sketch, "E251.third.point", {"position": v(-3.03, -45.37) * mm});
            skArc(sketch, "E252", {"start": v(-5.08, -45.99) * mm, "mid": v(-5.71, -45.35) * mm, "end": v(-6.35, -45.99) * mm});
            skPoint(sketch, "E252.third.point", {"position": v(-5.57, -45.37) * mm});
            skArc(sketch, "E253", {"start": v(-7.62, -45.99) * mm, "mid": v(-8.25, -45.35) * mm, "end": v(-8.89, -45.99) * mm});
            skPoint(sketch, "E253.third.point", {"position": v(-7.9, -45.47) * mm});
            skArc(sketch, "E254", {"start": v(-10.16, -45.99) * mm, "mid": v(-10.8, -45.35) * mm, "end": v(-11.43, -45.99) * mm});
            skPoint(sketch, "E254.third.point", {"position": v(-10.9, -45.36) * mm});
            skArc(sketch, "E255", {"start": v(-12.7, -45.99) * mm, "mid": v(-13.33, -45.35) * mm, "end": v(-13.97, -45.99) * mm});
            skPoint(sketch, "E255.third.point", {"position": v(-12.7, -45.99) * mm});
            skArc(sketch, "E256", {"start": v(-3.8, -52.45) * mm, "mid": v(-3.17, -53.08) * mm, "end": v(-2.54, -52.45) * mm});
            skPoint(sketch, "E256.second.point", {"position": v(-3.8, -52.45) * mm});
            skPoint(sketch, "E256.third.point", {"position": v(-3.17, -53.08) * mm});
            skArc(sketch, "E257", {"start": v(-6.35, -54.99) * mm, "mid": v(-5.71, -55.62) * mm, "end": v(-5.08, -54.99) * mm});
            skPoint(sketch, "E257.second.point", {"position": v(-6.35, -54.99) * mm});
            skPoint(sketch, "E257.third.point", {"position": v(-5.99, -55.56) * mm});
            skPoint(sketch, "E258.second.point", {"position": v(-7.62, -56.26) * mm});
            skArc(sketch, "E259", {"start": v(-8.89, -57.53) * mm, "mid": v(-8.25, -58.16) * mm, "end": v(-7.62, -57.53) * mm});
            skPoint(sketch, "E259.second.point", {"position": v(-8.89, -57.53) * mm});
            skPoint(sketch, "E259.third.point", {"position": v(-8.18, -58.16) * mm});
            skArc(sketch, "E260", {"start": v(-11.43, -59.33) * mm, "mid": v(-10.8, -59.96) * mm, "end": v(-10.16, -59.33) * mm});
            skPoint(sketch, "E260.third.point", {"position": v(-10.84, -59.96) * mm});
            skArc(sketch, "E261", {"start": v(-13.97, -59.33) * mm, "mid": v(-13.34, -59.96) * mm, "end": v(-12.7, -59.33) * mm});
            skPoint(sketch, "E261.third.point", {"position": v(-13.3, -59.96) * mm});
            skLineSegment(sketch, "E262", {"start": v(-15.87, -45.99) * mm, "end": v(-15.87, -59.33) * mm});
            skLineSegment(sketch, "E263", {"start": v(-14.99, -45.99) * mm, "end": v(-14.99, -59.33) * mm});
            skPoint(sketch, "E264.orphan", {"position": v(-16.5, -45.99) * mm});
            skPoint(sketch, "E265.orphan", {"position": v(-15.87, -45.57) * mm});
            skPoint(sketch, "E266.orphan", {"position": v(-14.99, -45.5) * mm});
            skArc(sketch, "E267", {"start": v(-14.99, -45.99) * mm, "mid": v(-15.43, -45.54) * mm, "end": v(-15.87, -45.99) * mm});
            skPoint(sketch, "E267.third.point", {"position": v(-15.47, -46.43) * mm});
            skArc(sketch, "E268", {"start": v(-15.87, -59.33) * mm, "mid": v(-15.43, -59.77) * mm, "end": v(-14.99, -59.33) * mm});
            skPoint(sketch, "E268.third.point", {"position": v(-14.99, -59.33) * mm});
            skPoint(sketch, "E269.orphan", {"position": v(-6.35, -56.26) * mm});
            skLineSegment(sketch, "E270.trimOffspring", {"start": v(-13.97, -59.33) * mm, "end": v(-12.7, -59.33) * mm});
            skLineSegment(sketch, "E271.trimOffspring", {"start": v(-11.43, -59.33) * mm, "end": v(-10.16, -59.33) * mm});
            skArc(sketch, "E272.MirrorCS", {"start": v(14.99, -45.99) * mm, "mid": v(15.43, -45.54) * mm, "end": v(15.88, -45.99) * mm});
            skArc(sketch, "E273.MirrorCS", {"start": v(12.7, -45.99) * mm, "mid": v(13.34, -45.35) * mm, "end": v(13.97, -45.99) * mm});
            skArc(sketch, "E274.MirrorCS", {"start": v(2.54, -45.99) * mm, "mid": v(3.18, -45.35) * mm, "end": v(3.81, -45.99) * mm});
            skPoint(sketch, "E275.MirrorP", {"position": v(15.88, -45.57) * mm});
            skArc(sketch, "E276.MirrorCS", {"start": v(7.62, -45.99) * mm, "mid": v(8.26, -45.35) * mm, "end": v(8.9, -45.99) * mm});
            skArc(sketch, "E277.MirrorCS", {"start": v(10.16, -45.99) * mm, "mid": v(10.8, -45.35) * mm, "end": v(11.43, -45.99) * mm});
            skPoint(sketch, "E278.MirrorP", {"position": v(7.62, -44.72) * mm});
            skPoint(sketch, "E279.MirrorP", {"position": v(16.51, -45.99) * mm});
            skPoint(sketch, "E280.MirrorP", {"position": v(15.24, -44.72) * mm});
            skPoint(sketch, "E281.MirrorP", {"position": v(13.97, -44.72) * mm});
            skArc(sketch, "E282.MirrorCS", {"start": v(5.08, -45.99) * mm, "mid": v(5.72, -45.35) * mm, "end": v(6.35, -45.99) * mm});
            skLineSegment(sketch, "E283.MirrorCS", {"start": v(10.16, -45.99) * mm, "end": v(10.16, -59.33) * mm});
            skLineSegment(sketch, "E284.MirrorCS", {"start": v(15.87, -45.99) * mm, "end": v(15.87, -59.33) * mm});
            skLineSegment(sketch, "E285.MirrorCS", {"start": v(8.9, -45.99) * mm, "end": v(8.89, -57.53) * mm});
            skPoint(sketch, "E286.MirrorP", {"position": v(14.99, -45.5) * mm});
            skLineSegment(sketch, "E287.MirrorCS", {"start": v(12.7, -45.99) * mm, "end": v(12.7, -59.33) * mm});
            skPoint(sketch, "E288.MirrorP", {"position": v(12.7, -45.99) * mm});
            skPoint(sketch, "E289.MirrorP", {"position": v(3.81, -44.72) * mm});
            skLineSegment(sketch, "E290.MirrorCS", {"start": v(2.54, -45.99) * mm, "end": v(2.54, -52.45) * mm});
            skLineSegment(sketch, "E291.MirrorCS", {"start": v(7.62, -45.99) * mm, "end": v(7.62, -57.53) * mm});
            skPoint(sketch, "E292.MirrorP", {"position": v(5.57, -45.37) * mm});
            skPoint(sketch, "E293.MirrorP", {"position": v(11.43, -44.72) * mm});
            skLineSegment(sketch, "E294.MirrorCS", {"start": v(14.99, -45.99) * mm, "end": v(14.99, -59.33) * mm});
            skPoint(sketch, "E295.MirrorP", {"position": v(6.35, -44.72) * mm});
            skPoint(sketch, "E296.MirrorP", {"position": v(15.47, -46.43) * mm});
            skLineSegment(sketch, "E297.MirrorCS", {"start": v(5.08, -45.99) * mm, "end": v(5.08, -54.99) * mm});
            skPoint(sketch, "E298.MirrorP", {"position": v(7.9, -45.47) * mm});
            skLineSegment(sketch, "E299.MirrorCS", {"start": v(11.43, -45.99) * mm, "end": v(11.43, -59.33) * mm});
            skPoint(sketch, "E300.MirrorP", {"position": v(10.16, -44.72) * mm});
            skPoint(sketch, "E301.MirrorP", {"position": v(12.7, -44.72) * mm});
            skPoint(sketch, "E302.MirrorP", {"position": v(3.03, -45.37) * mm});
            skPoint(sketch, "E303.MirrorP", {"position": v(8.9, -44.72) * mm});
            skPoint(sketch, "E304.MirrorP", {"position": v(10.9, -45.36) * mm});
            skLineSegment(sketch, "E305.MirrorCS", {"start": v(3.81, -45.99) * mm, "end": v(3.81, -52.45) * mm});
            skPoint(sketch, "E306.MirrorP", {"position": v(5.08, -44.72) * mm});
            skLineSegment(sketch, "E307.MirrorCS", {"start": v(13.97, -45.99) * mm, "end": v(13.97, -59.33) * mm});
            skLineSegment(sketch, "E308.MirrorCS", {"start": v(6.35, -45.99) * mm, "end": v(6.35, -54.99) * mm});
            skArc(sketch, "E309.MirrorCS", {"start": v(3.81, -52.45) * mm, "mid": v(3.18, -53.08) * mm, "end": v(2.54, -52.45) * mm});
            skArc(sketch, "E310.MirrorCS", {"start": v(6.35, -54.99) * mm, "mid": v(5.71, -55.62) * mm, "end": v(5.08, -54.99) * mm});
            skPoint(sketch, "E311.MirrorP", {"position": v(8.18, -58.16) * mm});
            skPoint(sketch, "E312.MirrorP", {"position": v(10.84, -59.96) * mm});
            skArc(sketch, "E313.MirrorCS", {"start": v(15.87, -59.33) * mm, "mid": v(15.43, -59.77) * mm, "end": v(14.99, -59.33) * mm});
            skArc(sketch, "E314.MirrorCS", {"start": v(13.97, -59.33) * mm, "mid": v(13.33, -59.96) * mm, "end": v(12.7, -59.33) * mm});
            skArc(sketch, "E315.MirrorCS", {"start": v(11.43, -59.33) * mm, "mid": v(10.8, -59.96) * mm, "end": v(10.16, -59.33) * mm});
            skArc(sketch, "E316.MirrorCS", {"start": v(8.89, -57.53) * mm, "mid": v(8.25, -58.16) * mm, "end": v(7.62, -57.53) * mm});
            skArc(sketch, "E317.trimOffspring", {"start": v(-5.87, -17.27) * mm, "mid": v(-5.08, -14.95) * mm, "end": v(-5.87, -12.62) * mm});
            skArc(sketch, "E318.trimOffspring", {"start": v(5.87, -17.27) * mm, "mid": v(5.08, -14.95) * mm, "end": v(5.87, -12.62) * mm});
            skArc(sketch, "E319.trimOffspring", {"start": v(-5.87, -31.62) * mm, "mid": v(-5.08, -33.95) * mm, "end": v(-5.87, -36.27) * mm});
            skArc(sketch, "E320.trimOffspring", {"start": v(5.87, -31.62) * mm, "mid": v(5.08, -33.95) * mm, "end": v(5.87, -36.27) * mm});
            skSolve(sketch);
        }
        {
            var Q0;
            Q0=makeQuery(id+"F44.imprint","IMPRINT",FACE,{"disambiguationData":[TD([[makeQuery(id+"F44.imprint","IMPRINT",EDGE,{"derivedFrom":sQuery(id+"F44.wireOp",EDGE,"E138.right")}),-1.0]])]});
            var Q1;
            Q1=makeQuery(id+"F44.imprint","IMPRINT",FACE,{"disambiguationData":[TD([[makeQuery(id+"F44.imprint","IMPRINT",EDGE,{"derivedFrom":sQuery(id+"F44.wireOp",EDGE,"E138.bottom")}),-1.0]])]});
            var Q2;
            Q2=makeQuery(id+"F44.imprint","IMPRINT",FACE,{"disambiguationData":[TD([[makeQuery(id+"F44.imprint","IMPRINT",EDGE,{"derivedFrom":sQuery(id+"F44.wireOp",EDGE,"E191.MirrorCS")}),1.0]])]});
            var Q3;
            Q3=makeQuery(id+"F44.imprint","IMPRINT",FACE,{"disambiguationData":[TD([[makeQuery(id+"F44.imprint","IMPRINT",EDGE,{"derivedFrom":sQuery(id+"F44.wireOp",EDGE,"E196.MirrorCS")}),-1.0]])]});
            var Q4;
            Q4=makeQuery(id+"F44.imprint","IMPRINT",FACE,{"disambiguationData":[TD([[makeQuery(id+"F44.imprint","IMPRINT",EDGE,{"derivedFrom":sQuery(id+"F44.wireOp",EDGE,"E138.top")}),1.0]])]});
            var Q5;
            Q5=makeQuery(id+"F44.imprint","IMPRINT",FACE,{"disambiguationData":[TD([[makeQuery(id+"F44.imprint","IMPRINT",EDGE,{"derivedFrom":sQuery(id+"F44.wireOp",EDGE,"E145.MirrorCS")}),-1.0]])]});
            var Q6;
            Q6=makeQuery(id+"F44.imprint","IMPRINT",FACE,{"disambiguationData":[TD([[makeQuery(id+"F44.imprint","IMPRINT",EDGE,{"derivedFrom":sQuery(id+"F44.wireOp",EDGE,"E146")}),1.0]])]});
            extrude(context, id + "F45", {"entities" : qUnion([Q0, Q1, Q2, Q3, Q4, Q5, Q6]), "operationType" : NewBodyOperationType.ADD, "depth" : 1.02 * mm});
        }
        {
            var Q0;
            Q0=makeQuery(id+"F45.boolean.opBoolean","SPLIT",FACE,{"disambiguationData":[TD([makeQuery(id+"F45.opExtrude","SWEPT_FACE",FACE,{"disambiguationData":[OSD([sQuery(id+"F44.wireOp",EDGE,"E262")])]})])],"derivedFrom":makeQuery(id+"F14.boolean.opBoolean","COPY",FACE,{"derivedFrom":makeQuery(id+"F14.opExtrude","SWEPT_FACE",FACE,{"disambiguationData":[OSD([sQuery(id+"F13.wireOp",EDGE,"E45.0")])]})})});
            var Q1;
            Q1=makeQuery(id+"F45.boolean.opBoolean","SPLIT",FACE,{"disambiguationData":[TD([makeQuery(id+"F45.opExtrude","SWEPT_FACE",FACE,{"disambiguationData":[OSD([sQuery(id+"F44.wireOp",EDGE,"E234.1.0.0")])]})])],"derivedFrom":makeQuery(id+"F14.boolean.opBoolean","COPY",FACE,{"derivedFrom":makeQuery(id+"F14.opExtrude","SWEPT_FACE",FACE,{"disambiguationData":[OSD([sQuery(id+"F13.wireOp",EDGE,"E45.0")])]})})});
            var Q2;
            Q2=makeQuery(id+"F45.boolean.opBoolean","SPLIT",FACE,{"disambiguationData":[TD([makeQuery(id+"F45.opExtrude","SWEPT_FACE",FACE,{"disambiguationData":[OSD([sQuery(id+"F44.wireOp",EDGE,"E234.3.0.0")])]})])],"derivedFrom":makeQuery(id+"F14.boolean.opBoolean","COPY",FACE,{"derivedFrom":makeQuery(id+"F14.opExtrude","SWEPT_FACE",FACE,{"disambiguationData":[OSD([sQuery(id+"F13.wireOp",EDGE,"E45.0")])]})})});
            var Q3;
            Q3=makeQuery(id+"F45.boolean.opBoolean","SPLIT",FACE,{"disambiguationData":[TD([makeQuery(id+"F45.opExtrude","SWEPT_FACE",FACE,{"disambiguationData":[OSD([sQuery(id+"F44.wireOp",EDGE,"E234.5.0.0")])]})])],"derivedFrom":makeQuery(id+"F14.boolean.opBoolean","COPY",FACE,{"derivedFrom":makeQuery(id+"F14.opExtrude","SWEPT_FACE",FACE,{"disambiguationData":[OSD([sQuery(id+"F13.wireOp",EDGE,"E45.0")])]})})});
            var Q4;
            Q4=makeQuery(id+"F45.boolean.opBoolean","SPLIT",FACE,{"disambiguationData":[TD([makeQuery(id+"F45.opExtrude","SWEPT_FACE",FACE,{"disambiguationData":[OSD([sQuery(id+"F44.wireOp",EDGE,"E234.7.0.0")])]})])],"derivedFrom":makeQuery(id+"F14.boolean.opBoolean","COPY",FACE,{"derivedFrom":makeQuery(id+"F14.opExtrude","SWEPT_FACE",FACE,{"disambiguationData":[OSD([sQuery(id+"F13.wireOp",EDGE,"E45.0")])]})})});
            var Q5;
            Q5=makeQuery(id+"F45.boolean.opBoolean","SPLIT",FACE,{"disambiguationData":[TD([makeQuery(id+"F45.opExtrude","SWEPT_FACE",FACE,{"disambiguationData":[OSD([sQuery(id+"F44.wireOp",EDGE,"E233.0")])]})])],"derivedFrom":makeQuery(id+"F14.boolean.opBoolean","COPY",FACE,{"derivedFrom":makeQuery(id+"F14.opExtrude","SWEPT_FACE",FACE,{"disambiguationData":[OSD([sQuery(id+"F13.wireOp",EDGE,"E45.0")])]})})});
            var Q6;
            Q6=makeQuery(id+"F45.boolean.opBoolean","SPLIT",FACE,{"disambiguationData":[TD([makeQuery(id+"F45.opExtrude","SWEPT_FACE",FACE,{"disambiguationData":[OSD([sQuery(id+"F44.wireOp",EDGE,"E274.MirrorCS")])]})])],"derivedFrom":makeQuery(id+"F14.boolean.opBoolean","COPY",FACE,{"derivedFrom":makeQuery(id+"F14.opExtrude","SWEPT_FACE",FACE,{"disambiguationData":[OSD([sQuery(id+"F13.wireOp",EDGE,"E45.0")])]})})});
            var Q7;
            Q7=makeQuery(id+"F45.boolean.opBoolean","SPLIT",FACE,{"disambiguationData":[TD([makeQuery(id+"F45.opExtrude","SWEPT_FACE",FACE,{"disambiguationData":[OSD([sQuery(id+"F44.wireOp",EDGE,"E282.MirrorCS")])]})])],"derivedFrom":makeQuery(id+"F14.boolean.opBoolean","COPY",FACE,{"derivedFrom":makeQuery(id+"F14.opExtrude","SWEPT_FACE",FACE,{"disambiguationData":[OSD([sQuery(id+"F13.wireOp",EDGE,"E45.0")])]})})});
            var Q8;
            Q8=makeQuery(id+"F45.boolean.opBoolean","SPLIT",FACE,{"disambiguationData":[TD([makeQuery(id+"F45.opExtrude","SWEPT_FACE",FACE,{"disambiguationData":[OSD([sQuery(id+"F44.wireOp",EDGE,"E276.MirrorCS")])]})])],"derivedFrom":makeQuery(id+"F14.boolean.opBoolean","COPY",FACE,{"derivedFrom":makeQuery(id+"F14.opExtrude","SWEPT_FACE",FACE,{"disambiguationData":[OSD([sQuery(id+"F13.wireOp",EDGE,"E45.0")])]})})});
            var Q9;
            Q9=makeQuery(id+"F45.boolean.opBoolean","SPLIT",FACE,{"disambiguationData":[TD([makeQuery(id+"F45.opExtrude","SWEPT_FACE",FACE,{"disambiguationData":[OSD([sQuery(id+"F44.wireOp",EDGE,"E277.MirrorCS")])]})])],"derivedFrom":makeQuery(id+"F14.boolean.opBoolean","COPY",FACE,{"derivedFrom":makeQuery(id+"F14.opExtrude","SWEPT_FACE",FACE,{"disambiguationData":[OSD([sQuery(id+"F13.wireOp",EDGE,"E45.0")])]})})});
            var Q10;
            Q10=makeQuery(id+"F45.boolean.opBoolean","SPLIT",FACE,{"disambiguationData":[TD([makeQuery(id+"F45.opExtrude","SWEPT_FACE",FACE,{"disambiguationData":[OSD([sQuery(id+"F44.wireOp",EDGE,"E273.MirrorCS")])]})])],"derivedFrom":makeQuery(id+"F14.boolean.opBoolean","COPY",FACE,{"derivedFrom":makeQuery(id+"F14.opExtrude","SWEPT_FACE",FACE,{"disambiguationData":[OSD([sQuery(id+"F13.wireOp",EDGE,"E45.0")])]})})});
            var Q11;
            Q11=makeQuery(id+"F45.boolean.opBoolean","SPLIT",FACE,{"disambiguationData":[TD([makeQuery(id+"F45.opExtrude","SWEPT_FACE",FACE,{"disambiguationData":[OSD([sQuery(id+"F44.wireOp",EDGE,"E272.MirrorCS")])]})])],"derivedFrom":makeQuery(id+"F14.boolean.opBoolean","COPY",FACE,{"derivedFrom":makeQuery(id+"F14.opExtrude","SWEPT_FACE",FACE,{"disambiguationData":[OSD([sQuery(id+"F13.wireOp",EDGE,"E45.0")])]})})});
            extrude(context, id + "F46", {"entities" : qUnion([Q0, Q1, Q2, Q3, Q4, Q5, Q6, Q7, Q8, Q9, Q10, Q11]), "operationType" : NewBodyOperationType.REMOVE, "oppositeDirection" : true, "depth" : 3.17 * mm});
        }
        {
            var Q0;
            Q0=makeQuery(id+"F45.opExtrude","CAP_EDGE",EDGE,{"disambiguationData":[OSD([sQuery(id+"F44.wireOp",EDGE,"E146")])],"isStart":false});
            fillet(context, id + "F47", {"entities" : qUnion([Q0]), "radius" : 2.54 * mm, "tangentPropagation" : true, "allowEdgeOverflow" : false});
        }
        {
            var Q0;
            Q0=makeQuery(id+"F14.boolean.opBoolean","COPY",FACE,{"derivedFrom":makeQuery(id+"F14.opExtrude","SWEPT_FACE",FACE,{"disambiguationData":[OSD([sQuery(id+"F13.wireOp",EDGE,"E41")])]})});
            var sketch = newSketch(context, id + "F48", { "sketchPlane" : qUnion([Q0])});
            skLineSegment(sketch, "E321", {"start": v(-19.05, 96.7) * mm, "end": v(-19.05, 4.14) * mm});
            skLineSegment(sketch, "E322", {"start": v(19.05, 96.7) * mm, "end": v(19.05, 4.14) * mm});
            skLineSegment(sketch, "E323", {"start": v(19.05, 4.14) * mm, "end": v(-19.05, 4.14) * mm});
            skLineSegment(sketch, "E324", {"start": v(-19.05, 96.7) * mm, "end": v(19.05, 96.7) * mm});
            skLineSegment(sketch, "E325.0", {"start": v(-16.5, 95.43) * mm, "end": v(16.5, 95.43) * mm});
            skLineSegment(sketch, "E326.0", {"start": v(-16.5, 95.43) * mm, "end": v(-16.5, 76.38) * mm});
            skLineSegment(sketch, "E327.0", {"start": v(16.5, 95.43) * mm, "end": v(16.5, 76.38) * mm});
            skLineSegment(sketch, "E328.0", {"start": v(16.5, 6.68) * mm, "end": v(8.89, 6.68) * mm});
            skLineSegment(sketch, "E329", {"start": v(27.23, 73.84) * mm, "end": v(27.23, 21.92) * mm});
            skPoint(sketch, "E330.endSnap0", {"position": v(27.23, 47.88) * mm});
            skLineSegment(sketch, "E331.0", {"start": v(27.23, 49.15) * mm, "end": v(19.05, 49.15) * mm});
            skLineSegment(sketch, "E332.0", {"start": v(27.23, 46.61) * mm, "end": v(19.05, 46.61) * mm});
            skLineSegment(sketch, "E333.trimOffspring", {"start": v(-16.5, 19.38) * mm, "end": v(-8.89, 19.38) * mm});
            skLineSegment(sketch, "E334.trimOffspring", {"start": v(-16.5, 21.92) * mm, "end": v(-1.27, 21.92) * mm});
            skLineSegment(sketch, "E335.trimOffspring", {"start": v(19.05, 19.38) * mm, "end": v(35.4, 19.38) * mm});
            skLineSegment(sketch, "E336.trimOffspring", {"start": v(19.05, 21.92) * mm, "end": v(35.4, 21.92) * mm});
            skPoint(sketch, "E337.orphan", {"position": v(0, 6.68) * mm});
            skLineSegment(sketch, "E338.trimOffspring", {"start": v(1.27, 21.92) * mm, "end": v(16.5, 21.92) * mm});
            skLineSegment(sketch, "E339.trimOffspring", {"start": v(-16.5, 19.38) * mm, "end": v(-16.5, 6.68) * mm});
            skLineSegment(sketch, "E340.trimOffspring", {"start": v(-16.5, 46.61) * mm, "end": v(-16.5, 21.92) * mm});
            skLineSegment(sketch, "E341.trimOffspring", {"start": v(-1.27, 46.61) * mm, "end": v(-1.27, 21.92) * mm});
            skLineSegment(sketch, "E342.trimOffspring", {"start": v(1.27, 46.61) * mm, "end": v(1.27, 21.92) * mm});
            skLineSegment(sketch, "E343.trimOffspring", {"start": v(-1.27, 46.61) * mm, "end": v(-16.5, 46.61) * mm});
            skLineSegment(sketch, "E344.trimOffspring", {"start": v(16.5, 19.38) * mm, "end": v(16.5, 6.68) * mm});
            skLineSegment(sketch, "E345.trimOffspring", {"start": v(16.5, 46.61) * mm, "end": v(16.5, 21.92) * mm});
            skLineSegment(sketch, "E346.trimOffspring", {"start": v(16.5, 46.61) * mm, "end": v(1.27, 46.61) * mm});
            skLineSegment(sketch, "E347.trimOffspring", {"start": v(16.5, 49.15) * mm, "end": v(1.27, 49.15) * mm});
            skLineSegment(sketch, "E348.trimOffspring", {"start": v(-1.27, 49.15) * mm, "end": v(-16.5, 49.15) * mm});
            skLineSegment(sketch, "E349.trimOffspring", {"start": v(-1.27, 73.84) * mm, "end": v(-1.27, 49.15) * mm});
            skLineSegment(sketch, "E350.trimOffspring", {"start": v(0, 73.84) * mm, "end": v(0, 21.92) * mm});
            skLineSegment(sketch, "E351.trimOffspring", {"start": v(1.27, 73.84) * mm, "end": v(1.27, 49.15) * mm});
            skLineSegment(sketch, "E352.trimOffspring", {"start": v(1.27, 73.84) * mm, "end": v(16.5, 73.84) * mm});
            skLineSegment(sketch, "E353.trimOffspring", {"start": v(-16.5, 73.84) * mm, "end": v(-1.27, 73.84) * mm});
            skLineSegment(sketch, "E354.trimOffspring", {"start": v(-16.5, 76.38) * mm, "end": v(16.5, 76.38) * mm});
            skLineSegment(sketch, "E355.trimOffspring", {"start": v(19.05, 73.84) * mm, "end": v(27.23, 73.84) * mm});
            skLineSegment(sketch, "E356.trimOffspring", {"start": v(19.05, 76.38) * mm, "end": v(27.23, 76.38) * mm});
            skLineSegment(sketch, "E357.trimOffspring", {"start": v(16.5, 73.84) * mm, "end": v(16.5, 49.15) * mm});
            skLineSegment(sketch, "E358.trimOffspring", {"start": v(-16.5, 73.84) * mm, "end": v(-16.5, 49.15) * mm});
            skPoint(sketch, "E359.orphan", {"position": v(-19.05, 95.43) * mm});
            skLineSegment(sketch, "E360.0", {"start": v(-8.89, 6.68) * mm, "end": v(-8.89, 19.38) * mm});
            skLineSegment(sketch, "E361.0", {"start": v(-7.62, 6.68) * mm, "end": v(-7.62, 19.38) * mm});
            skLineSegment(sketch, "E362.0", {"start": v(0.64, 6.68) * mm, "end": v(0.64, 19.38) * mm});
            skLineSegment(sketch, "E363.0", {"start": v(-0.63, 6.68) * mm, "end": v(-0.63, 19.38) * mm});
            skPoint(sketch, "E364.end.orphan", {"position": v(0, 19.38) * mm});
            skLineSegment(sketch, "E365.MirrorCS", {"start": v(7.62, 6.68) * mm, "end": v(7.62, 19.38) * mm});
            skLineSegment(sketch, "E366.MirrorCS", {"start": v(8.89, 6.68) * mm, "end": v(8.89, 19.38) * mm});
            skLineSegment(sketch, "E367.trimOffspring", {"start": v(-7.62, 19.38) * mm, "end": v(-0.63, 19.38) * mm});
            skLineSegment(sketch, "E368.trimOffspring", {"start": v(-8.89, 6.68) * mm, "end": v(-16.5, 6.68) * mm});
            skLineSegment(sketch, "E369.trimOffspring", {"start": v(-0.63, 6.68) * mm, "end": v(-7.62, 6.68) * mm});
            skLineSegment(sketch, "E370.trimOffspring", {"start": v(0.64, 19.38) * mm, "end": v(7.62, 19.38) * mm});
            skLineSegment(sketch, "E371.trimOffspring", {"start": v(7.62, 6.68) * mm, "end": v(0.64, 6.68) * mm});
            skLineSegment(sketch, "E372.trimOffspring", {"start": v(8.89, 19.38) * mm, "end": v(16.5, 19.38) * mm});
            skPoint(sketch, "E373.orphan", {"position": v(19.05, 6.68) * mm});
            skPoint(sketch, "E374.orphan", {"position": v(19.05, 95.43) * mm});
            skSolve(sketch);
        }
        {
            var Q0;
            Q0=makeQuery(id+"F48.imprint","IMPRINT",FACE,{"disambiguationData":[TD([[makeQuery(id+"F48.imprint","IMPRINT",EDGE,{"derivedFrom":sQuery(id+"F48.wireOp",EDGE,"E328.0")}),-1.0]])]});
            var Q1;
            Q1=makeQuery(id+"F48.imprint","IMPRINT",FACE,{"disambiguationData":[TD([[makeQuery(id+"F48.imprint","IMPRINT",EDGE,{"derivedFrom":sQuery(id+"F48.wireOp",EDGE,"E362.0")}),-1.0]])]});
            var Q2;
            Q2=makeQuery(id+"F48.imprint","IMPRINT",FACE,{"disambiguationData":[TD([[makeQuery(id+"F48.imprint","IMPRINT",EDGE,{"derivedFrom":sQuery(id+"F48.wireOp",EDGE,"E361.0")}),-1.0]])]});
            var Q3;
            Q3=makeQuery(id+"F48.imprint","IMPRINT",FACE,{"disambiguationData":[TD([[makeQuery(id+"F48.imprint","IMPRINT",EDGE,{"derivedFrom":sQuery(id+"F48.wireOp",EDGE,"E333.trimOffspring")}),-1.0]])]});
            var Q4;
            Q4=makeQuery(id+"F48.imprint","IMPRINT",FACE,{"disambiguationData":[TD([[makeQuery(id+"F48.imprint","IMPRINT",EDGE,{"derivedFrom":sQuery(id+"F48.wireOp",EDGE,"E334.trimOffspring")}),1.0]])]});
            var Q5;
            Q5=makeQuery(id+"F48.imprint","IMPRINT",FACE,{"disambiguationData":[TD([[makeQuery(id+"F48.imprint","IMPRINT",EDGE,{"derivedFrom":sQuery(id+"F48.wireOp",EDGE,"E338.trimOffspring")}),1.0]])]});
            var Q6;
            Q6=makeQuery(id+"F48.imprint","IMPRINT",FACE,{"disambiguationData":[TD([[makeQuery(id+"F48.imprint","IMPRINT",EDGE,{"derivedFrom":sQuery(id+"F48.wireOp",EDGE,"E347.trimOffspring")}),-1.0]])]});
            var Q7;
            Q7=makeQuery(id+"F48.imprint","IMPRINT",FACE,{"disambiguationData":[TD([[makeQuery(id+"F48.imprint","IMPRINT",EDGE,{"derivedFrom":sQuery(id+"F48.wireOp",EDGE,"E348.trimOffspring")}),-1.0]])]});
            var Q8;
            Q8=makeQuery(id+"F48.imprint","IMPRINT",FACE,{"disambiguationData":[TD([[makeQuery(id+"F48.imprint","IMPRINT",EDGE,{"derivedFrom":sQuery(id+"F48.wireOp",EDGE,"E325.0")}),-1.0]])]});
            extrude(context, id + "F49", {"entities" : qUnion([Q0, Q1, Q2, Q3, Q4, Q5, Q6, Q7, Q8]), "operationType" : NewBodyOperationType.ADD, "depth" : 1.27 * mm, "symmetric" : true});
        }
        {
            var Q0;
            Q0=makeQuery(id+"F14.boolean.opBoolean","COPY",FACE,{"derivedFrom":makeQuery(id+"F14.opExtrude","SWEPT_FACE",FACE,{"disambiguationData":[OSD([sQuery(id+"F13.wireOp",EDGE,"E42")])]})});
            var sketch = newSketch(context, id + "F50", { "sketchPlane" : qUnion([Q0])});
            skLineSegment(sketch, "E375", {"start": v(-19.05, 53.06) * mm, "end": v(-19.05, 70.16) * mm});
            skLineSegment(sketch, "E376", {"start": v(-19.05, 70.16) * mm, "end": v(19.05, 70.16) * mm});
            skLineSegment(sketch, "E377", {"start": v(19.05, 70.16) * mm, "end": v(19.05, 53.06) * mm});
            skLineSegment(sketch, "E378", {"start": v(19.05, 53.06) * mm, "end": v(-19.05, 53.06) * mm});
            skLineSegment(sketch, "E379.0", {"start": v(-16.5, 55.6) * mm, "end": v(-16.5, 67.62) * mm});
            skLineSegment(sketch, "E380.0", {"start": v(16.5, 67.62) * mm, "end": v(16.5, 55.6) * mm});
            skLineSegment(sketch, "E381.0", {"start": v(16.5, 55.6) * mm, "end": v(-16.5, 55.6) * mm});
            skLineSegment(sketch, "E382.0", {"start": v(-16.5, 67.62) * mm, "end": v(16.5, 67.62) * mm});
            skSolve(sketch);
        }
        {
            var Q0;
            Q0=makeQuery(id+"F50.imprint","IMPRINT",FACE,{"disambiguationData":[TD([[makeQuery(id+"F50.imprint","IMPRINT",EDGE,{"derivedFrom":sQuery(id+"F50.wireOp",EDGE,"E379.0")}),-1.0]])]});
            extrude(context, id + "F51", {"entities" : qUnion([Q0]), "operationType" : NewBodyOperationType.REMOVE, "oppositeDirection" : true, "depth" : 3.17 * mm});
        }
        {
            var Q0;
            Q0=makeQuery(id+"F14.boolean.opBoolean","COPY",FACE,{"derivedFrom":makeQuery(id+"F14.opExtrude","SWEPT_FACE",FACE,{"disambiguationData":[OSD([sQuery(id+"F13.wireOp",EDGE,"E44")])]})});
            var sketch = newSketch(context, id + "F52", { "sketchPlane" : qUnion([Q0])});
            skLineSegment(sketch, "E383.0", {"start": v(16.5, 8.26) * mm, "end": v(0.63, 8.26) * mm});
            skLineSegment(sketch, "E384.0", {"start": v(-16.5, -2.45) * mm, "end": v(-1.27, -2.45) * mm});
            skLineSegment(sketch, "E385.0", {"start": v(-16.5, 8.25) * mm, "end": v(-16.5, -2.45) * mm});
            skLineSegment(sketch, "E386.0", {"start": v(16.51, -2.45) * mm, "end": v(16.5, 8.26) * mm});
            skPoint(sketch, "E387.orphan", {"position": v(-0.63, -2.45) * mm});
            skPoint(sketch, "E388.orphan", {"position": v(0, -1.18) * mm});
            skPoint(sketch, "E389.orphan", {"position": v(0.64, -1.18) * mm});
            skPoint(sketch, "E390.orphan", {"position": v(-0.63, 8.25) * mm});
            skPoint(sketch, "E391.start.orphan", {"position": v(0, 8.26) * mm});
            skPoint(sketch, "E392.orphan", {"position": v(-16.5, -1.18) * mm});
            skPoint(sketch, "E393.orphan", {"position": v(16.51, -1.18) * mm});
            skLineSegment(sketch, "E394", {"start": v(-0.63, 2.9) * mm, "end": v(-0.63, 8.25) * mm});
            skLineSegment(sketch, "E395", {"start": v(0.63, 2.9) * mm, "end": v(0.63, 8.26) * mm});
            skLineSegment(sketch, "E396", {"start": v(-0.63, 2.9) * mm, "end": v(-1.27, -2.45) * mm});
            skLineSegment(sketch, "E397", {"start": v(0.63, 2.9) * mm, "end": v(1.27, -2.45) * mm});
            skPoint(sketch, "E398.orphan", {"position": v(-16.5, 2.9) * mm});
            skLineSegment(sketch, "E399.trimOffspring", {"start": v(16.51, 2.9) * mm, "end": v(17.22, 2.9) * mm});
            skLineSegment(sketch, "E400.trimOffspring", {"start": v(-0.63, 8.26) * mm, "end": v(-16.51, 8.25) * mm});
            skLineSegment(sketch, "E401.trimOffspring", {"start": v(1.27, -2.45) * mm, "end": v(16.51, -2.45) * mm});
            skSolve(sketch);
        }
        {
            var Q0;
            Q0 = qSketchRegion(id + "F52", true);
            extrude(context, id + "F53", {"entities" : qUnion([Q0]), "operationType" : NewBodyOperationType.ADD, "depth" : 1.02 * mm});
        }
        {
            var Q0;
            Q0=makeQuery(id+"F50.imprint","IMPRINT",FACE,{"disambiguationData":[TD([[makeQuery(id+"F50.imprint","IMPRINT",EDGE,{"derivedFrom":sQuery(id+"F50.wireOp",EDGE,"E379.0")}),-1.0]])]});
            extrude(context, id + "F54", {"entities" : qUnion([Q0]), "depth" : 3.17 * mm});
        }
        {
            var Q0;
            Q0=makeQuery(id+"F54.opExtrude","CAP_FACE",FACE,{"disambiguationData":[OSD([sQuery(id+"F50.wireOp",EDGE,"E379.0"),sQuery(id+"F50.wireOp",EDGE,"E380.0"),sQuery(id+"F50.wireOp",EDGE,"E381.0"),sQuery(id+"F50.wireOp",EDGE,"E382.0")])],"isStart":false});
            fillet(context, id + "F55", {"entities" : qUnion([Q0]), "radius" : 3.17 * mm, "tangentPropagation" : true, "allowEdgeOverflow" : false});
        }
        {
            var Q0;
            Q0=makeQuery(id+"F43.opExtrude","CAP_FACE",FACE,{"disambiguationData":[OSD([sQuery(id+"F41.wireOp",EDGE,"E137")])],"isStart":false});
            var sketch = newSketch(context, id + "F56", { "sketchPlane" : qUnion([Q0])});
            skLineSegment(sketch, "E402", {"start": v(0, 0) * mm, "end": v(0, 3.18) * mm});
            skCircle(sketch, "E403", {"center": v(107.95, 3.18) * mm, "radius": 33.34 * mm});
            skLineSegment(sketch, "E404.0", {"start": v(132.53, 23.27) * mm, "end": v(133.66, 24.4) * mm});
            skLineSegment(sketch, "E405.0", {"start": v(128.04, 27.76) * mm, "end": v(129.17, 28.89) * mm});
            skArc(sketch, "E406", {"start": v(98.8, 33.58) * mm, "mid": v(95.8, 32.5) * mm, "end": v(92.93, 31.15) * mm});
            skLineSegment(sketch, "E407.1.0", {"start": v(117.1, 33.58) * mm, "end": v(117.72, 35.05) * mm});
            skLineSegment(sketch, "E407.1.1", {"start": v(122.97, 31.15) * mm, "end": v(123.58, 32.62) * mm});
            skLineSegment(sketch, "E407.2.0", {"start": v(104.77, 34.77) * mm, "end": v(104.77, 36.36) * mm});
            skLineSegment(sketch, "E407.2.1", {"start": v(111.12, 34.77) * mm, "end": v(111.12, 36.36) * mm});
            skLineSegment(sketch, "E408.1.3.0", {"start": v(92.93, 31.15) * mm, "end": v(92.32, 32.62) * mm});
            skLineSegment(sketch, "E408.3.3.0", {"start": v(98.8, 33.58) * mm, "end": v(98.18, 35.05) * mm});
            skLineSegment(sketch, "E409.1.4.0", {"start": v(83.37, 23.27) * mm, "end": v(82.24, 24.4) * mm});
            skLineSegment(sketch, "E409.3.4.0", {"start": v(87.86, 27.76) * mm, "end": v(86.73, 28.89) * mm});
            skLineSegment(sketch, "E409.1.5.0", {"start": v(77.55, 12.33) * mm, "end": v(76.08, 12.94) * mm});
            skLineSegment(sketch, "E409.3.5.0", {"start": v(79.98, 18.2) * mm, "end": v(78.5, 18.8) * mm});
            skLineSegment(sketch, "E409.1.6.0", {"start": v(76.36, 0) * mm, "end": v(74.76, 0) * mm});
            skLineSegment(sketch, "E409.3.6.0", {"start": v(76.36, 6.35) * mm, "end": v(74.76, 6.35) * mm});
            skLineSegment(sketch, "E409.1.7.0", {"start": v(79.98, -11.85) * mm, "end": v(78.5, -12.46) * mm});
            skLineSegment(sketch, "E409.3.7.0", {"start": v(77.55, -5.98) * mm, "end": v(76.08, -6.6) * mm});
            skLineSegment(sketch, "E410.1.8.0", {"start": v(87.86, -21.4) * mm, "end": v(86.73, -22.54) * mm});
            skLineSegment(sketch, "E410.3.8.0", {"start": v(83.37, -16.92) * mm, "end": v(82.24, -18.05) * mm});
            skLineSegment(sketch, "E410.1.9.0", {"start": v(98.8, -27.23) * mm, "end": v(98.18, -28.7) * mm});
            skLineSegment(sketch, "E410.3.9.0", {"start": v(92.93, -24.8) * mm, "end": v(92.32, -26.27) * mm});
            skLineSegment(sketch, "E410.1.10.0", {"start": v(111.13, -28.42) * mm, "end": v(111.13, -30.01) * mm});
            skLineSegment(sketch, "E410.3.10.0", {"start": v(104.78, -28.42) * mm, "end": v(104.78, -30.01) * mm});
            skLineSegment(sketch, "E410.1.11.0", {"start": v(122.97, -24.8) * mm, "end": v(123.58, -26.27) * mm});
            skLineSegment(sketch, "E410.3.11.0", {"start": v(117.1, -27.23) * mm, "end": v(117.72, -28.7) * mm});
            skLineSegment(sketch, "E410.1.12.0", {"start": v(132.53, -16.92) * mm, "end": v(133.66, -18.05) * mm});
            skLineSegment(sketch, "E410.3.12.0", {"start": v(128.04, -21.4) * mm, "end": v(129.17, -22.54) * mm});
            skLineSegment(sketch, "E410.1.13.0", {"start": v(138.35, -5.98) * mm, "end": v(139.82, -6.6) * mm});
            skLineSegment(sketch, "E410.3.13.0", {"start": v(135.92, -11.85) * mm, "end": v(137.4, -12.46) * mm});
            skLineSegment(sketch, "E410.1.14.0", {"start": v(139.54, 6.35) * mm, "end": v(141.14, 6.35) * mm});
            skLineSegment(sketch, "E410.3.14.0", {"start": v(139.54, 0) * mm, "end": v(141.14, 0) * mm});
            skLineSegment(sketch, "E410.1.15.0", {"start": v(135.92, 18.2) * mm, "end": v(137.4, 18.8) * mm});
            skLineSegment(sketch, "E410.3.15.0", {"start": v(138.35, 12.33) * mm, "end": v(139.82, 12.94) * mm});
            skArc(sketch, "E411.trimOffspring", {"start": v(111.12, 34.77) * mm, "mid": v(107.95, 34.93) * mm, "end": v(104.77, 34.77) * mm});
            skArc(sketch, "E412.trimOffspring", {"start": v(122.97, 31.15) * mm, "mid": v(120.1, 32.5) * mm, "end": v(117.1, 33.58) * mm});
            skArc(sketch, "E413.trimOffspring", {"start": v(132.53, 23.27) * mm, "mid": v(130.4, 25.63) * mm, "end": v(128.04, 27.76) * mm});
            skArc(sketch, "E414.trimOffspring", {"start": v(138.35, 12.33) * mm, "mid": v(137.28, 15.33) * mm, "end": v(135.92, 18.2) * mm});
            skArc(sketch, "E415.trimOffspring", {"start": v(139.54, 0) * mm, "mid": v(139.7, 3.18) * mm, "end": v(139.54, 6.35) * mm});
            skArc(sketch, "E416.trimOffspring", {"start": v(135.92, -11.85) * mm, "mid": v(137.28, -8.98) * mm, "end": v(138.35, -5.98) * mm});
            skArc(sketch, "E417.trimOffspring", {"start": v(128.04, -21.4) * mm, "mid": v(130.4, -19.28) * mm, "end": v(132.53, -16.92) * mm});
            skArc(sketch, "E418.trimOffspring", {"start": v(117.1, -27.23) * mm, "mid": v(120.1, -26.16) * mm, "end": v(122.97, -24.8) * mm});
            skArc(sketch, "E419.trimOffspring", {"start": v(104.77, -28.42) * mm, "mid": v(107.95, -28.57) * mm, "end": v(111.12, -28.42) * mm});
            skArc(sketch, "E420.trimOffspring", {"start": v(92.93, -24.8) * mm, "mid": v(95.8, -26.16) * mm, "end": v(98.8, -27.23) * mm});
            skArc(sketch, "E421.trimOffspring", {"start": v(83.37, -16.92) * mm, "mid": v(85.5, -19.28) * mm, "end": v(87.86, -21.4) * mm});
            skArc(sketch, "E422.trimOffspring", {"start": v(77.55, -5.98) * mm, "mid": v(78.62, -8.98) * mm, "end": v(79.98, -11.85) * mm});
            skArc(sketch, "E423.trimOffspring", {"start": v(76.36, 6.35) * mm, "mid": v(76.2, 3.18) * mm, "end": v(76.36, 0) * mm});
            skArc(sketch, "E424.trimOffspring", {"start": v(79.98, 18.2) * mm, "mid": v(78.62, 15.33) * mm, "end": v(77.55, 12.33) * mm});
            skArc(sketch, "E425.trimOffspring", {"start": v(87.86, 27.76) * mm, "mid": v(85.5, 25.63) * mm, "end": v(83.37, 23.27) * mm});
            skSolve(sketch);
        }
        {
            var Q0;
            Q0=makeQuery(id+"F43.opExtrude","CAP_FACE",FACE,{"disambiguationData":[OSD([sQuery(id+"F41.wireOp",EDGE,"E137")])],"isStart":false});
            var sketch = newSketch(context, id + "F57", { "sketchPlane" : qUnion([Q0])});
            skCircle(sketch, "E426", {"center": v(107.95, 3.18) * mm, "radius": 33.34 * mm});
            skSolve(sketch);
        }
        {
            var Q0;
            {var subQ0=sQuery(id+"F56.wireOp",EDGE,"E409.1.4.0");Q0=makeQuery(id+"F56.imprint","IMPRINT",FACE,{"disambiguationData":[TD([[makeQuery(id+"F56.imprint","IMPRINT",EDGE,{"derivedFrom":subQ0}),-1.0]])]});}
            var Q1;
            {var subQ0=sQuery(id+"F56.wireOp",EDGE,"E409.1.5.0");Q1=makeQuery(id+"F56.imprint","IMPRINT",FACE,{"disambiguationData":[TD([[makeQuery(id+"F56.imprint","IMPRINT",EDGE,{"derivedFrom":subQ0}),-1.0]])]});}
            var Q2;
            {var subQ0=sQuery(id+"F56.wireOp",EDGE,"E409.1.7.0");Q2=makeQuery(id+"F56.imprint","IMPRINT",FACE,{"disambiguationData":[TD([[makeQuery(id+"F56.imprint","IMPRINT",EDGE,{"derivedFrom":subQ0}),-1.0]])]});}
            var Q3;
            {var subQ0=sQuery(id+"F56.wireOp",EDGE,"E409.1.6.0");Q3=makeQuery(id+"F56.imprint","IMPRINT",FACE,{"disambiguationData":[TD([[makeQuery(id+"F56.imprint","IMPRINT",EDGE,{"derivedFrom":subQ0}),-1.0]])]});}
            var Q4;
            {var subQ0=sQuery(id+"F56.wireOp",EDGE,"E410.1.8.0");Q4=makeQuery(id+"F56.imprint","IMPRINT",FACE,{"disambiguationData":[TD([[makeQuery(id+"F56.imprint","IMPRINT",EDGE,{"derivedFrom":subQ0}),-1.0]])]});}
            var Q5;
            Q5=makeQuery(id+"F56.imprint","IMPRINT",FACE,{"disambiguationData":[TD([[makeQuery(id+"F56.imprint","IMPRINT",EDGE,{"derivedFrom":sQuery(id+"F56.wireOp",EDGE,"E406")}),-1.0]])]});
            var Q6;
            {var subQ0=sQuery(id+"F56.wireOp",EDGE,"E407.2.0");Q6=makeQuery(id+"F56.imprint","IMPRINT",FACE,{"disambiguationData":[TD([[makeQuery(id+"F56.imprint","IMPRINT",EDGE,{"derivedFrom":subQ0}),-1.0]])]});}
            var Q7;
            {var subQ0=sQuery(id+"F56.wireOp",EDGE,"E407.1.0");Q7=makeQuery(id+"F56.imprint","IMPRINT",FACE,{"disambiguationData":[TD([[makeQuery(id+"F56.imprint","IMPRINT",EDGE,{"derivedFrom":subQ0}),-1.0]])]});}
            var Q8;
            {var subQ0=sQuery(id+"F56.wireOp",EDGE,"E404.0");Q8=makeQuery(id+"F56.imprint","IMPRINT",FACE,{"disambiguationData":[TD([[makeQuery(id+"F56.imprint","IMPRINT",EDGE,{"derivedFrom":subQ0}),1.0]])]});}
            var Q9;
            {var subQ0=sQuery(id+"F56.wireOp",EDGE,"E410.1.15.0");Q9=makeQuery(id+"F56.imprint","IMPRINT",FACE,{"disambiguationData":[TD([[makeQuery(id+"F56.imprint","IMPRINT",EDGE,{"derivedFrom":subQ0}),-1.0]])]});}
            var Q10;
            {var subQ0=sQuery(id+"F56.wireOp",EDGE,"E410.1.14.0");Q10=makeQuery(id+"F56.imprint","IMPRINT",FACE,{"disambiguationData":[TD([[makeQuery(id+"F56.imprint","IMPRINT",EDGE,{"derivedFrom":subQ0}),-1.0]])]});}
            var Q11;
            {var subQ0=sQuery(id+"F56.wireOp",EDGE,"E410.1.13.0");Q11=makeQuery(id+"F56.imprint","IMPRINT",FACE,{"disambiguationData":[TD([[makeQuery(id+"F56.imprint","IMPRINT",EDGE,{"derivedFrom":subQ0}),-1.0]])]});}
            var Q12;
            {var subQ0=sQuery(id+"F56.wireOp",EDGE,"E410.1.12.0");Q12=makeQuery(id+"F56.imprint","IMPRINT",FACE,{"disambiguationData":[TD([[makeQuery(id+"F56.imprint","IMPRINT",EDGE,{"derivedFrom":subQ0}),-1.0]])]});}
            var Q13;
            {var subQ0=sQuery(id+"F56.wireOp",EDGE,"E410.1.11.0");Q13=makeQuery(id+"F56.imprint","IMPRINT",FACE,{"disambiguationData":[TD([[makeQuery(id+"F56.imprint","IMPRINT",EDGE,{"derivedFrom":subQ0}),-1.0]])]});}
            var Q14;
            {var subQ0=sQuery(id+"F56.wireOp",EDGE,"E410.1.10.0");Q14=makeQuery(id+"F56.imprint","IMPRINT",FACE,{"disambiguationData":[TD([[makeQuery(id+"F56.imprint","IMPRINT",EDGE,{"derivedFrom":subQ0}),-1.0]])]});}
            var Q15;
            {var subQ0=sQuery(id+"F56.wireOp",EDGE,"E410.1.9.0");Q15=makeQuery(id+"F56.imprint","IMPRINT",FACE,{"disambiguationData":[TD([[makeQuery(id+"F56.imprint","IMPRINT",EDGE,{"derivedFrom":subQ0}),-1.0]])]});}
            extrude(context, id + "F58", {"entities" : qUnion([Q0, Q1, Q2, Q3, Q4, Q5, Q6, Q7, Q8, Q9, Q10, Q11, Q12, Q13, Q14, Q15]), "operationType" : NewBodyOperationType.REMOVE, "oppositeDirection" : true, "depth" : 3.57 * mm});
        }
        {
            var Q0;
            Q0 = qSketchRegion(id + "F57", true);
            extrude(context, id + "F59", {"entities" : qUnion([Q0]), "operationType" : NewBodyOperationType.ADD, "oppositeDirection" : true, "depth" : 1.2 * mm});
        }
        {
            var Q0;
            Q0=makeQuery(id+"F43.opExtrude","SWEPT_BODY",BODY,{"disambiguationData":[OSD([sQuery(id+"F41.wireOp",EDGE,"E137")])]});
            var Q1;
            Q1=qCreatedBy(makeId("Right.planeOp"),FACE);
            mirror(context, id + "F60", {"entities" : qUnion([Q0]), "mirrorPlane" : qUnion([Q1])});
        }
        {
            var Q0;
            Q0=makeQuery(id+"F59.boolean.opBoolean","MERGE",FACE,{"derivedFrom":[makeQuery(id+"F43.opExtrude","CAP_FACE",FACE,{"disambiguationData":[OSD([sQuery(id+"F41.wireOp",EDGE,"E137")])],"isStart":false}),makeQuery(id+"F59.opExtrude","CAP_FACE",FACE,{"disambiguationData":[OSD([sQuery(id+"F57.wireOp",EDGE,"E426")])],"isStart":true})]});
            var sketch = newSketch(context, id + "F61", { "sketchPlane" : qUnion([Q0])});
            skLineSegment(sketch, "E427", {"start": v(0, 3.18) * mm, "end": v(107.95, 3.18) * mm});
            skCircle(sketch, "E428", {"center": v(107.95, 3.18) * mm, "radius": 6.35 * mm});
            skSolve(sketch);
        }
        {
            var Q0;
            Q0=sQuery(id+"F61.wireOp",VERTEX,"E428.center");
            var Q1;
            Q1=makeQuery(id+"F9.opExtrude","SWEPT_BODY",BODY,{"disambiguationData":[OSD([sQuery(id+"F6.wireOp",EDGE,"E0"),sQuery(id+"F6.wireOp",EDGE,"E12"),sQuery(id+"F6.wireOp",EDGE,"E13"),sQuery(id+"F6.wireOp",EDGE,"E14")])]});
            var Q2;
            Q2=makeQuery(id+"F7.opExtrude","SWEPT_BODY",BODY,{"disambiguationData":[OSD([sQuery(id+"F6.wireOp",EDGE,"E2"),sQuery(id+"F6.wireOp",EDGE,"E3"),sQuery(id+"F6.wireOp",EDGE,"E4"),sQuery(id+"F6.wireOp",EDGE,"E12"),sQuery(id+"F6.wireOp",EDGE,"E13"),sQuery(id+"F6.wireOp",EDGE,"E14"),sQuery(id+"F6.wireOp",EDGE,"E15"),sQuery(id+"F6.wireOp",EDGE,"E16"),sQuery(id+"F6.wireOp",EDGE,"E17"),sQuery(id+"F6.wireOp",EDGE,"E18")])]});
            hole(context, id + "F62", {"style" : HoleStyle.SIMPLE, "endStyle" : HoleEndStyle.BLIND, "holeDiameter" : 12.7 * mm, "holeDepth" : 152.4 * mm, "tappedDepth" : 12.7 * mm, "tapClearance" : 3, "locations" : qUnion([Q0]), "scope" : qUnion([Q1, Q2])});
        }
    });
